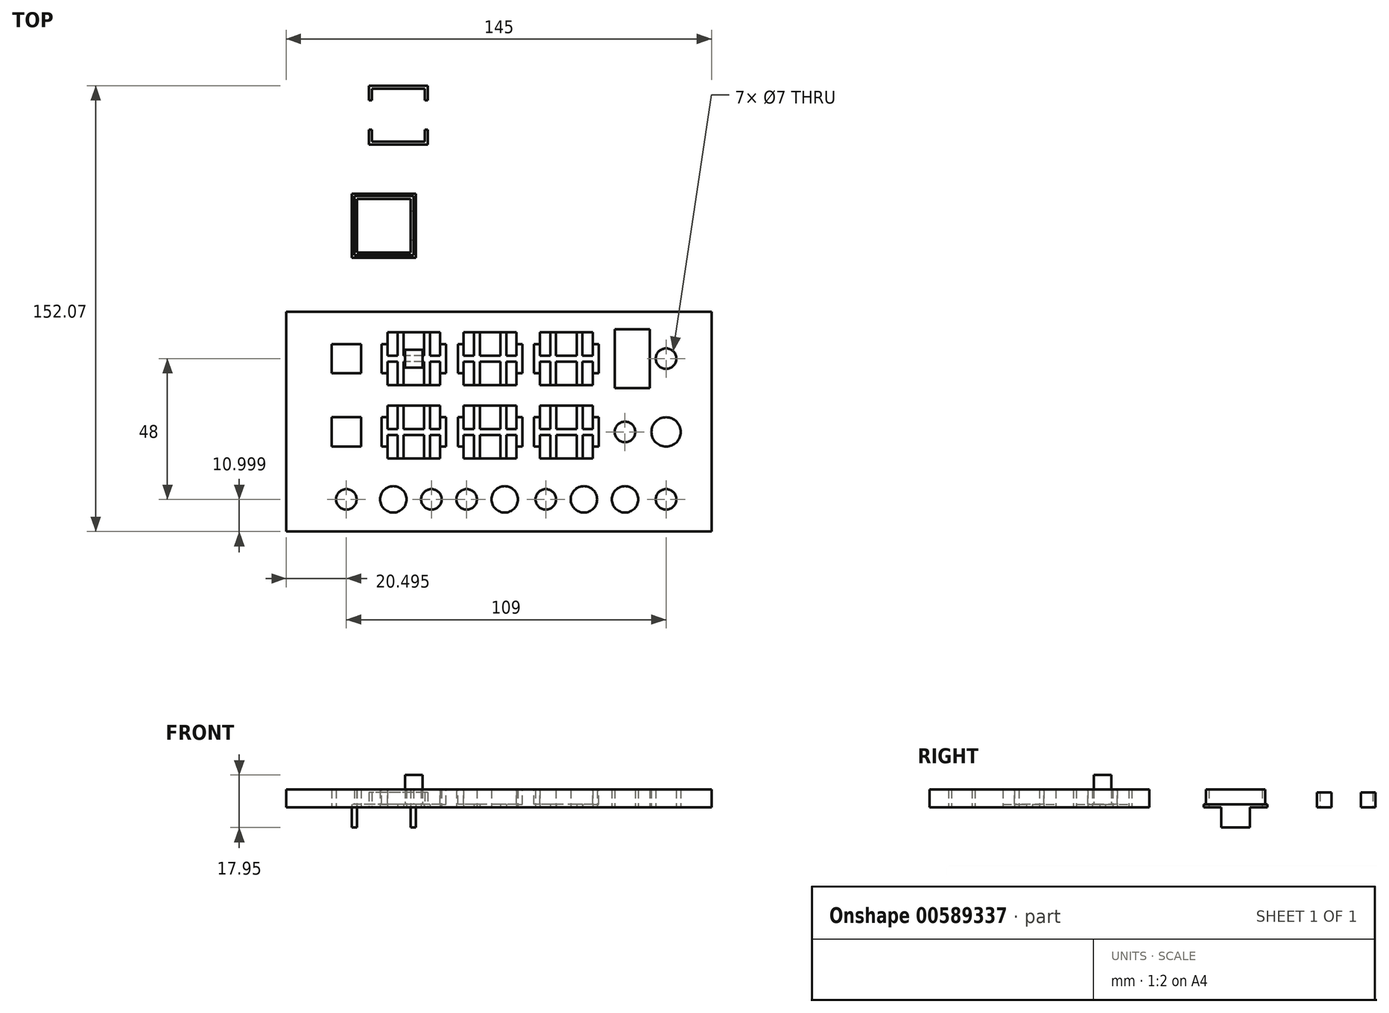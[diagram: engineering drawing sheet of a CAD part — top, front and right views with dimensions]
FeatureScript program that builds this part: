
annotation { "Feature Type Name" : "Feature", "Feature Type Description" : "" }
export const myFeature = defineFeature(function(context is Context, id is Id, definition is map)
    precondition{}
    {
        {
            var Q0;
            Q0=qCreatedBy(makeId("Top.planeOp"),FACE);
            var sketch = newSketch(context, id + "F0", { "sketchPlane" : qUnion([Q0])});
            skLineSegment(sketch, "E0.bottom", {"start": v(-10, -55.04) * mm, "end": v(-155, -55.04) * mm});
            skLineSegment(sketch, "E0.top", {"start": v(-10, 19.96) * mm, "end": v(-155, 19.96) * mm});
            skLineSegment(sketch, "E0.left", {"start": v(-10, -55.04) * mm, "end": v(-10, 19.96) * mm});
            skLineSegment(sketch, "E0.right", {"start": v(-155, -55.04) * mm, "end": v(-155, 19.96) * mm});
            skPoint(sketch, "E0.middle", {"position": v(-82.5, -17.54) * mm});
            skLineSegment(sketch, "E1.bottom", {"start": v(-101.5, -6.04) * mm, "end": v(-121.5, -6.04) * mm, "construction": true});
            skLineSegment(sketch, "E1.top", {"start": v(-101.5, 13.96) * mm, "end": v(-121.5, 13.96) * mm, "construction": true});
            skLineSegment(sketch, "E1.left", {"start": v(-101.5, -6.04) * mm, "end": v(-101.5, 13.96) * mm, "construction": true});
            skLineSegment(sketch, "E1.right", {"start": v(-121.5, -6.04) * mm, "end": v(-121.5, 13.96) * mm, "construction": true});
            skPoint(sketch, "E1.middle", {"position": v(-111.5, 3.96) * mm});
            skLineSegment(sketch, "E2.1.0.0", {"start": v(-95.5, -6.04) * mm, "end": v(-95.5, 13.96) * mm, "construction": true});
            skPoint(sketch, "E2.1.0.1", {"position": v(-85.5, 3.96) * mm});
            skLineSegment(sketch, "E2.1.0.2", {"start": v(-75.5, -6.04) * mm, "end": v(-95.5, -6.04) * mm, "construction": true});
            skLineSegment(sketch, "E2.1.0.3", {"start": v(-75.5, -6.04) * mm, "end": v(-75.5, 13.96) * mm, "construction": true});
            skLineSegment(sketch, "E2.1.0.4", {"start": v(-75.5, 13.96) * mm, "end": v(-95.5, 13.96) * mm, "construction": true});
            skLineSegment(sketch, "E2.2.0.0", {"start": v(-69.5, -6.04) * mm, "end": v(-69.5, 13.96) * mm, "construction": true});
            skPoint(sketch, "E2.2.0.1", {"position": v(-59.5, 3.96) * mm});
            skLineSegment(sketch, "E2.2.0.2", {"start": v(-49.5, -6.04) * mm, "end": v(-69.5, -6.04) * mm, "construction": true});
            skLineSegment(sketch, "E2.2.0.3", {"start": v(-49.5, -6.04) * mm, "end": v(-49.5, 13.96) * mm, "construction": true});
            skLineSegment(sketch, "E2.2.0.4", {"start": v(-49.5, 13.96) * mm, "end": v(-69.5, 13.96) * mm, "construction": true});
            skLineSegment(sketch, "E2.direction1", {"start": v(-121.5, -6.04) * mm, "end": v(-95.5, -6.04) * mm, "construction": true});
            skLineSegment(sketch, "E3.bottom", {"start": v(-101.5, -31.04) * mm, "end": v(-121.5, -31.04) * mm, "construction": true});
            skLineSegment(sketch, "E3.top", {"start": v(-101.5, -11.04) * mm, "end": v(-121.5, -11.04) * mm, "construction": true});
            skLineSegment(sketch, "E3.left", {"start": v(-101.5, -31.04) * mm, "end": v(-101.5, -11.04) * mm, "construction": true});
            skLineSegment(sketch, "E3.right", {"start": v(-121.5, -31.04) * mm, "end": v(-121.5, -11.04) * mm, "construction": true});
            skPoint(sketch, "E3.middle", {"position": v(-111.5, -21.04) * mm});
            skLineSegment(sketch, "E4.1.0.0", {"start": v(-75.5, -31.04) * mm, "end": v(-95.5, -31.04) * mm, "construction": true});
            skLineSegment(sketch, "E4.1.0.1", {"start": v(-75.5, -31.04) * mm, "end": v(-75.5, -11.04) * mm, "construction": true});
            skLineSegment(sketch, "E4.1.0.2", {"start": v(-95.5, -31.04) * mm, "end": v(-95.5, -11.04) * mm, "construction": true});
            skLineSegment(sketch, "E4.1.0.3", {"start": v(-75.5, -11.04) * mm, "end": v(-95.5, -11.04) * mm, "construction": true});
            skPoint(sketch, "E4.1.0.4", {"position": v(-85.5, -21.04) * mm});
            skLineSegment(sketch, "E4.2.0.0", {"start": v(-49.5, -31.04) * mm, "end": v(-69.5, -31.04) * mm, "construction": true});
            skLineSegment(sketch, "E4.2.0.1", {"start": v(-49.5, -31.04) * mm, "end": v(-49.5, -11.04) * mm, "construction": true});
            skLineSegment(sketch, "E4.2.0.2", {"start": v(-69.5, -31.04) * mm, "end": v(-69.5, -11.04) * mm, "construction": true});
            skLineSegment(sketch, "E4.2.0.3", {"start": v(-49.5, -11.04) * mm, "end": v(-69.5, -11.04) * mm, "construction": true});
            skPoint(sketch, "E4.2.0.4", {"position": v(-59.5, -21.04) * mm});
            skLineSegment(sketch, "E4.direction1", {"start": v(-121.5, -31.04) * mm, "end": v(-95.5, -31.04) * mm, "construction": true});
            skCircle(sketch, "E5", {"center": v(-134.5, -44.04) * mm, "radius": 3.5 * mm});
            skCircle(sketch, "E6", {"center": v(-105.5, -44.04) * mm, "radius": 3.5 * mm});
            skCircle(sketch, "E7", {"center": v(-93.5, -44.04) * mm, "radius": 3.5 * mm});
            skLineSegment(sketch, "E8.bottom", {"start": v(-155, 19.96) * mm, "end": v(-147, 19.96) * mm, "construction": true});
            skLineSegment(sketch, "E8.top", {"start": v(-155, -55.04) * mm, "end": v(-147, -55.04) * mm, "construction": true});
            skLineSegment(sketch, "E8.left", {"start": v(-155, 19.96) * mm, "end": v(-155, -55.04) * mm, "construction": true});
            skLineSegment(sketch, "E8.right", {"start": v(-147, 19.96) * mm, "end": v(-147, -55.04) * mm, "construction": true});
            skLineSegment(sketch, "E9.bottom", {"start": v(-10, -55.04) * mm, "end": v(-18, -55.04) * mm, "construction": true});
            skLineSegment(sketch, "E9.top", {"start": v(-10, 19.96) * mm, "end": v(-18, 19.96) * mm, "construction": true});
            skLineSegment(sketch, "E9.left", {"start": v(-10, -55.04) * mm, "end": v(-10, 19.96) * mm, "construction": true});
            skLineSegment(sketch, "E9.right", {"start": v(-18, -55.04) * mm, "end": v(-18, 19.96) * mm, "construction": true});
            skCircle(sketch, "E10", {"center": v(-118.5, -44.04) * mm, "radius": 4.5 * mm});
            skCircle(sketch, "E11", {"center": v(-80.5, -44.04) * mm, "radius": 4.5 * mm});
            skCircle(sketch, "E12", {"center": v(-66.5, -44.04) * mm, "radius": 3.5 * mm});
            skCircle(sketch, "E13", {"center": v(-53.5, -44.04) * mm, "radius": 4.5 * mm});
            skCircle(sketch, "E14", {"center": v(-39.5, -44.04) * mm, "radius": 4.5 * mm});
            skCircle(sketch, "E15", {"center": v(-25.5, -44.04) * mm, "radius": 3.5 * mm});
            skCircle(sketch, "E16", {"center": v(-39.5, -21.04) * mm, "radius": 3.5 * mm});
            skLineSegment(sketch, "E17.bottom", {"start": v(-31, -6.04) * mm, "end": v(-43, -6.04) * mm});
            skLineSegment(sketch, "E17.top", {"start": v(-31, 13.96) * mm, "end": v(-43, 13.96) * mm});
            skLineSegment(sketch, "E17.left", {"start": v(-31, -6.04) * mm, "end": v(-31, 13.96) * mm});
            skLineSegment(sketch, "E17.right", {"start": v(-43, -6.04) * mm, "end": v(-43, 13.96) * mm});
            skPoint(sketch, "E17.middle", {"position": v(-37, 3.96) * mm});
            skCircle(sketch, "E18", {"center": v(-25.5, 3.96) * mm, "radius": 3.5 * mm});
            skCircle(sketch, "E19", {"center": v(-25.5, -21.04) * mm, "radius": 5 * mm});
            skPoint(sketch, "E20.centerSnap0", {"position": v(-121.5, -21.04) * mm});
            skLineSegment(sketch, "E21.bottom", {"start": v(-102.5, -5.04) * mm, "end": v(-120.5, -5.04) * mm});
            skLineSegment(sketch, "E21.top", {"start": v(-102.5, 12.96) * mm, "end": v(-120.5, 12.96) * mm});
            skLineSegment(sketch, "E21.left", {"start": v(-102.5, -5.04) * mm, "end": v(-102.5, 12.96) * mm});
            skLineSegment(sketch, "E21.right", {"start": v(-120.5, -5.04) * mm, "end": v(-120.5, 12.96) * mm});
            skLineSegment(sketch, "E22.bottom", {"start": v(-102.5, -30.04) * mm, "end": v(-120.5, -30.04) * mm});
            skLineSegment(sketch, "E22.top", {"start": v(-102.5, -12.04) * mm, "end": v(-120.5, -12.04) * mm});
            skLineSegment(sketch, "E22.left", {"start": v(-102.5, -30.04) * mm, "end": v(-102.5, -12.04) * mm});
            skLineSegment(sketch, "E22.right", {"start": v(-120.5, -30.04) * mm, "end": v(-120.5, -12.04) * mm});
            skLineSegment(sketch, "E23.bottom", {"start": v(-102.5, 2.96) * mm, "end": v(-106, 2.96) * mm});
            skLineSegment(sketch, "E23.top", {"start": v(-102.5, 4.96) * mm, "end": v(-106, 4.96) * mm});
            skLineSegment(sketch, "E23.left", {"start": v(-102.5, 2.96) * mm, "end": v(-102.5, 4.96) * mm});
            skLineSegment(sketch, "E23.right", {"start": v(-120.5, 2.96) * mm, "end": v(-120.5, 4.96) * mm});
            skLineSegment(sketch, "E24.bottom", {"start": v(-115, -5.04) * mm, "end": v(-117, -5.04) * mm});
            skLineSegment(sketch, "E24.top", {"start": v(-115, 12.96) * mm, "end": v(-117, 12.96) * mm});
            skLineSegment(sketch, "E24.left", {"start": v(-115, -5.04) * mm, "end": v(-115, 2.96) * mm});
            skLineSegment(sketch, "E24.right", {"start": v(-117, -5.04) * mm, "end": v(-117, 2.96) * mm});
            skPoint(sketch, "E24.middle", {"position": v(-116, 3.96) * mm});
            skLineSegment(sketch, "E25.bottom", {"start": v(-106, -5.04) * mm, "end": v(-108, -5.04) * mm});
            skLineSegment(sketch, "E25.top", {"start": v(-106, 12.96) * mm, "end": v(-108, 12.96) * mm});
            skLineSegment(sketch, "E25.left", {"start": v(-106, -5.04) * mm, "end": v(-106, 2.96) * mm});
            skLineSegment(sketch, "E25.right", {"start": v(-108, -5.04) * mm, "end": v(-108, 2.96) * mm});
            skPoint(sketch, "E25.middle", {"position": v(-107, 3.96) * mm});
            skLineSegment(sketch, "E26.trimOffspring", {"start": v(-117, 4.96) * mm, "end": v(-117, 12.96) * mm});
            skLineSegment(sketch, "E27.trimOffspring", {"start": v(-117, 4.96) * mm, "end": v(-120.5, 4.96) * mm});
            skLineSegment(sketch, "E28.trimOffspring", {"start": v(-115, 4.96) * mm, "end": v(-115, 12.96) * mm});
            skLineSegment(sketch, "E29.trimOffspring", {"start": v(-117, 2.96) * mm, "end": v(-120.5, 2.96) * mm});
            skLineSegment(sketch, "E30.trimOffspring", {"start": v(-108, 4.96) * mm, "end": v(-108, 12.96) * mm});
            skLineSegment(sketch, "E31.trimOffspring", {"start": v(-108, 4.96) * mm, "end": v(-115, 4.96) * mm});
            skLineSegment(sketch, "E32.trimOffspring", {"start": v(-106, 4.96) * mm, "end": v(-106, 12.96) * mm});
            skLineSegment(sketch, "E33.trimOffspring", {"start": v(-108, 2.96) * mm, "end": v(-115, 2.96) * mm});
            skLineSegment(sketch, "E34.bottom", {"start": v(-131, -50.54) * mm, "end": v(-138, -50.54) * mm, "construction": true});
            skLineSegment(sketch, "E34.top", {"start": v(-131, -37.54) * mm, "end": v(-138, -37.54) * mm, "construction": true});
            skLineSegment(sketch, "E34.left", {"start": v(-131, -50.54) * mm, "end": v(-131, -37.54) * mm, "construction": true});
            skLineSegment(sketch, "E34.right", {"start": v(-138, -50.54) * mm, "end": v(-138, -37.54) * mm, "construction": true});
            skLineSegment(sketch, "E35.bottom", {"start": v(-102.5, -22.04) * mm, "end": v(-105.98, -22.04) * mm});
            skLineSegment(sketch, "E35.top", {"start": v(-102.5, -20.04) * mm, "end": v(-105.98, -20.04) * mm});
            skLineSegment(sketch, "E35.left", {"start": v(-102.5, -22.04) * mm, "end": v(-102.5, -20.04) * mm});
            skLineSegment(sketch, "E35.right", {"start": v(-120.5, -22.04) * mm, "end": v(-120.5, -20.04) * mm});
            skLineSegment(sketch, "E36.bottom", {"start": v(-114.98, -30.04) * mm, "end": v(-116.98, -30.04) * mm});
            skLineSegment(sketch, "E36.top", {"start": v(-114.98, -12.04) * mm, "end": v(-116.98, -12.04) * mm});
            skLineSegment(sketch, "E36.left", {"start": v(-114.98, -30.04) * mm, "end": v(-114.98, -22.04) * mm});
            skLineSegment(sketch, "E36.right", {"start": v(-116.98, -30.04) * mm, "end": v(-116.98, -22.04) * mm});
            skPoint(sketch, "E36.middle", {"position": v(-115.98, -21.04) * mm});
            skLineSegment(sketch, "E37.bottom", {"start": v(-105.98, -30.04) * mm, "end": v(-107.98, -30.04) * mm});
            skLineSegment(sketch, "E37.top", {"start": v(-105.98, -12.04) * mm, "end": v(-107.98, -12.04) * mm});
            skLineSegment(sketch, "E37.left", {"start": v(-105.98, -30.04) * mm, "end": v(-105.98, -22.04) * mm});
            skLineSegment(sketch, "E37.right", {"start": v(-107.98, -30.04) * mm, "end": v(-107.98, -22.04) * mm});
            skPoint(sketch, "E37.middle", {"position": v(-106.98, -21.04) * mm});
            skLineSegment(sketch, "E38.trimOffspring", {"start": v(-116.98, -20.04) * mm, "end": v(-116.98, -12.04) * mm});
            skLineSegment(sketch, "E39.trimOffspring", {"start": v(-116.98, -20.04) * mm, "end": v(-120.5, -20.04) * mm});
            skLineSegment(sketch, "E40.trimOffspring", {"start": v(-114.98, -20.04) * mm, "end": v(-114.98, -12.04) * mm});
            skLineSegment(sketch, "E41.trimOffspring", {"start": v(-116.98, -22.04) * mm, "end": v(-120.5, -22.04) * mm});
            skLineSegment(sketch, "E42.trimOffspring", {"start": v(-107.98, -20.04) * mm, "end": v(-107.98, -12.04) * mm});
            skLineSegment(sketch, "E43.trimOffspring", {"start": v(-107.98, -20.04) * mm, "end": v(-114.98, -20.04) * mm});
            skLineSegment(sketch, "E44.trimOffspring", {"start": v(-105.98, -20.04) * mm, "end": v(-105.98, -12.04) * mm});
            skLineSegment(sketch, "E45.trimOffspring", {"start": v(-107.98, -22.04) * mm, "end": v(-114.98, -22.04) * mm});
            skLineSegment(sketch, "E46.bottom", {"start": v(-129.5, -1.04) * mm, "end": v(-139.5, -1.04) * mm});
            skLineSegment(sketch, "E46.top", {"start": v(-129.5, 8.96) * mm, "end": v(-139.5, 8.96) * mm});
            skLineSegment(sketch, "E46.left", {"start": v(-129.5, -1.04) * mm, "end": v(-129.5, 8.96) * mm});
            skLineSegment(sketch, "E46.right", {"start": v(-139.5, -1.04) * mm, "end": v(-139.5, 8.96) * mm});
            skPoint(sketch, "E46.middle", {"position": v(-134.5, 3.96) * mm});
            skLineSegment(sketch, "E47.bottom", {"start": v(-129.5, -26.04) * mm, "end": v(-139.5, -26.04) * mm});
            skLineSegment(sketch, "E47.top", {"start": v(-129.5, -16.04) * mm, "end": v(-139.5, -16.04) * mm});
            skLineSegment(sketch, "E47.left", {"start": v(-129.5, -26.04) * mm, "end": v(-129.5, -16.04) * mm});
            skLineSegment(sketch, "E47.right", {"start": v(-139.5, -26.04) * mm, "end": v(-139.5, -16.04) * mm});
            skPoint(sketch, "E47.middle", {"position": v(-134.5, -21.04) * mm});
            skLineSegment(sketch, "E48.1.0.0", {"start": v(-91, 4.96) * mm, "end": v(-91, 12.96) * mm});
            skLineSegment(sketch, "E48.1.0.2", {"start": v(-76.5, -5.04) * mm, "end": v(-76.5, 12.96) * mm});
            skLineSegment(sketch, "E48.1.0.3", {"start": v(-80, -5.04) * mm, "end": v(-80, 2.96) * mm});
            skPoint(sketch, "E48.1.0.4", {"position": v(-90, 3.96) * mm});
            skLineSegment(sketch, "E48.1.0.5", {"start": v(-82, 4.96) * mm, "end": v(-82, 12.96) * mm});
            skLineSegment(sketch, "E48.1.0.6", {"start": v(-80, 4.96) * mm, "end": v(-80, 12.96) * mm});
            skLineSegment(sketch, "E48.1.0.7", {"start": v(-82, 4.96) * mm, "end": v(-89, 4.96) * mm});
            skLineSegment(sketch, "E48.1.0.8", {"start": v(-76.5, 4.96) * mm, "end": v(-80, 4.96) * mm});
            skLineSegment(sketch, "E48.1.0.9", {"start": v(-76.5, 2.96) * mm, "end": v(-80, 2.96) * mm});
            skLineSegment(sketch, "E48.1.0.10", {"start": v(-80, 12.96) * mm, "end": v(-82, 12.96) * mm});
            skPoint(sketch, "E48.1.0.11", {"position": v(-81, 3.96) * mm});
            skLineSegment(sketch, "E48.1.0.12", {"start": v(-91, 4.96) * mm, "end": v(-94.5, 4.96) * mm});
            skLineSegment(sketch, "E48.1.0.13", {"start": v(-91, 2.96) * mm, "end": v(-94.5, 2.96) * mm});
            skLineSegment(sketch, "E48.1.0.14", {"start": v(-89, 4.96) * mm, "end": v(-89, 12.96) * mm});
            skLineSegment(sketch, "E48.1.0.15", {"start": v(-76.5, 12.96) * mm, "end": v(-94.5, 12.96) * mm});
            skLineSegment(sketch, "E48.1.0.16", {"start": v(-91, -5.04) * mm, "end": v(-91, 2.96) * mm});
            skLineSegment(sketch, "E48.1.0.17", {"start": v(-76.5, -5.04) * mm, "end": v(-94.5, -5.04) * mm});
            skLineSegment(sketch, "E48.1.0.18", {"start": v(-89, -5.04) * mm, "end": v(-89, 2.96) * mm});
            skLineSegment(sketch, "E48.1.0.19", {"start": v(-82, -5.04) * mm, "end": v(-82, 2.96) * mm});
            skLineSegment(sketch, "E48.1.0.20", {"start": v(-94.5, -5.04) * mm, "end": v(-94.5, 12.96) * mm});
            skLineSegment(sketch, "E48.1.0.21", {"start": v(-82, 2.96) * mm, "end": v(-89, 2.96) * mm});
            skLineSegment(sketch, "E48.1.0.22", {"start": v(-80, -5.04) * mm, "end": v(-82, -5.04) * mm});
            skLineSegment(sketch, "E48.1.0.23", {"start": v(-76.5, 2.96) * mm, "end": v(-76.5, 4.96) * mm});
            skLineSegment(sketch, "E48.1.0.24", {"start": v(-89, -5.04) * mm, "end": v(-91, -5.04) * mm});
            skLineSegment(sketch, "E48.1.0.25", {"start": v(-94.5, 2.96) * mm, "end": v(-94.5, 4.96) * mm});
            skLineSegment(sketch, "E48.1.0.27", {"start": v(-89, 12.96) * mm, "end": v(-91, 12.96) * mm});
            skLineSegment(sketch, "E48.2.0.0", {"start": v(-65, 4.96) * mm, "end": v(-65, 12.96) * mm});
            skLineSegment(sketch, "E48.2.0.2", {"start": v(-50.5, -5.04) * mm, "end": v(-50.5, 12.96) * mm});
            skLineSegment(sketch, "E48.2.0.3", {"start": v(-54, -5.04) * mm, "end": v(-54, 2.96) * mm});
            skPoint(sketch, "E48.2.0.4", {"position": v(-64, 3.96) * mm});
            skLineSegment(sketch, "E48.2.0.5", {"start": v(-56, 4.96) * mm, "end": v(-56, 12.96) * mm});
            skLineSegment(sketch, "E48.2.0.6", {"start": v(-54, 4.96) * mm, "end": v(-54, 12.96) * mm});
            skLineSegment(sketch, "E48.2.0.7", {"start": v(-56, 4.96) * mm, "end": v(-63, 4.96) * mm});
            skLineSegment(sketch, "E48.2.0.8", {"start": v(-50.5, 4.96) * mm, "end": v(-54, 4.96) * mm});
            skLineSegment(sketch, "E48.2.0.9", {"start": v(-50.5, 2.96) * mm, "end": v(-54, 2.96) * mm});
            skLineSegment(sketch, "E48.2.0.10", {"start": v(-54, 12.96) * mm, "end": v(-56, 12.96) * mm});
            skPoint(sketch, "E48.2.0.11", {"position": v(-55, 3.96) * mm});
            skLineSegment(sketch, "E48.2.0.12", {"start": v(-65, 4.96) * mm, "end": v(-68.5, 4.96) * mm});
            skLineSegment(sketch, "E48.2.0.13", {"start": v(-65, 2.96) * mm, "end": v(-68.5, 2.96) * mm});
            skLineSegment(sketch, "E48.2.0.14", {"start": v(-63, 4.96) * mm, "end": v(-63, 12.96) * mm});
            skLineSegment(sketch, "E48.2.0.15", {"start": v(-50.5, 12.96) * mm, "end": v(-68.5, 12.96) * mm});
            skLineSegment(sketch, "E48.2.0.16", {"start": v(-65, -5.04) * mm, "end": v(-65, 2.96) * mm});
            skLineSegment(sketch, "E48.2.0.17", {"start": v(-50.5, -5.04) * mm, "end": v(-68.5, -5.04) * mm});
            skLineSegment(sketch, "E48.2.0.18", {"start": v(-63, -5.04) * mm, "end": v(-63, 2.96) * mm});
            skLineSegment(sketch, "E48.2.0.19", {"start": v(-56, -5.04) * mm, "end": v(-56, 2.96) * mm});
            skLineSegment(sketch, "E48.2.0.20", {"start": v(-68.5, -5.04) * mm, "end": v(-68.5, 12.96) * mm});
            skLineSegment(sketch, "E48.2.0.21", {"start": v(-56, 2.96) * mm, "end": v(-63, 2.96) * mm});
            skLineSegment(sketch, "E48.2.0.22", {"start": v(-54, -5.04) * mm, "end": v(-56, -5.04) * mm});
            skLineSegment(sketch, "E48.2.0.23", {"start": v(-50.5, 2.96) * mm, "end": v(-50.5, 4.96) * mm});
            skLineSegment(sketch, "E48.2.0.24", {"start": v(-63, -5.04) * mm, "end": v(-65, -5.04) * mm});
            skLineSegment(sketch, "E48.2.0.25", {"start": v(-68.5, 2.96) * mm, "end": v(-68.5, 4.96) * mm});
            skLineSegment(sketch, "E48.2.0.27", {"start": v(-63, 12.96) * mm, "end": v(-65, 12.96) * mm});
            skLineSegment(sketch, "E48.direction1", {"start": v(-120.5, -5.04) * mm, "end": v(-94.5, -5.04) * mm, "construction": true});
            skLineSegment(sketch, "E49.1.0.0", {"start": v(-76.5, -20.04) * mm, "end": v(-79.98, -20.04) * mm});
            skLineSegment(sketch, "E49.1.0.1", {"start": v(-88.98, -20.04) * mm, "end": v(-88.98, -12.04) * mm});
            skLineSegment(sketch, "E49.1.0.2", {"start": v(-81.98, -30.04) * mm, "end": v(-81.98, -22.04) * mm});
            skLineSegment(sketch, "E49.1.0.3", {"start": v(-94.5, -30.04) * mm, "end": v(-94.5, -12.04) * mm});
            skLineSegment(sketch, "E49.1.0.4", {"start": v(-90.98, -30.04) * mm, "end": v(-90.98, -22.04) * mm});
            skLineSegment(sketch, "E49.1.0.5", {"start": v(-76.5, -30.04) * mm, "end": v(-76.5, -12.04) * mm});
            skLineSegment(sketch, "E49.1.0.6", {"start": v(-81.98, -22.04) * mm, "end": v(-88.98, -22.04) * mm});
            skLineSegment(sketch, "E49.1.0.7", {"start": v(-88.98, -30.04) * mm, "end": v(-88.98, -22.04) * mm});
            skLineSegment(sketch, "E49.1.0.9", {"start": v(-79.98, -20.04) * mm, "end": v(-79.98, -12.04) * mm});
            skLineSegment(sketch, "E49.1.0.10", {"start": v(-76.5, -22.04) * mm, "end": v(-79.98, -22.04) * mm});
            skPoint(sketch, "E49.1.0.11", {"position": v(-80.98, -21.04) * mm});
            skLineSegment(sketch, "E49.1.0.12", {"start": v(-90.98, -22.04) * mm, "end": v(-94.5, -22.04) * mm});
            skLineSegment(sketch, "E49.1.0.14", {"start": v(-81.98, -20.04) * mm, "end": v(-88.98, -20.04) * mm});
            skPoint(sketch, "E49.1.0.15", {"position": v(-89.98, -21.04) * mm});
            skLineSegment(sketch, "E49.1.0.16", {"start": v(-79.98, -30.04) * mm, "end": v(-79.98, -22.04) * mm});
            skLineSegment(sketch, "E49.1.0.17", {"start": v(-76.5, -30.04) * mm, "end": v(-94.5, -30.04) * mm});
            skLineSegment(sketch, "E49.1.0.18", {"start": v(-90.98, -20.04) * mm, "end": v(-90.98, -12.04) * mm});
            skLineSegment(sketch, "E49.1.0.19", {"start": v(-81.98, -20.04) * mm, "end": v(-81.98, -12.04) * mm});
            skLineSegment(sketch, "E49.1.0.20", {"start": v(-90.98, -20.04) * mm, "end": v(-94.5, -20.04) * mm});
            skLineSegment(sketch, "E49.1.0.21", {"start": v(-76.5, -12.04) * mm, "end": v(-94.5, -12.04) * mm});
            skLineSegment(sketch, "E49.1.0.22", {"start": v(-88.98, -12.04) * mm, "end": v(-90.98, -12.04) * mm});
            skLineSegment(sketch, "E49.1.0.23", {"start": v(-76.5, -22.04) * mm, "end": v(-76.5, -20.04) * mm});
            skLineSegment(sketch, "E49.1.0.24", {"start": v(-94.5, -22.04) * mm, "end": v(-94.5, -20.04) * mm});
            skLineSegment(sketch, "E49.1.0.26", {"start": v(-94.5, -30.04) * mm, "end": v(-94.5, -12.04) * mm});
            skLineSegment(sketch, "E49.1.0.27", {"start": v(-79.98, -12.04) * mm, "end": v(-81.98, -12.04) * mm});
            skLineSegment(sketch, "E49.1.0.28", {"start": v(-76.5, -30.04) * mm, "end": v(-94.5, -30.04) * mm});
            skLineSegment(sketch, "E49.1.0.29", {"start": v(-76.5, -12.04) * mm, "end": v(-94.5, -12.04) * mm});
            skLineSegment(sketch, "E49.1.0.30", {"start": v(-76.5, -30.04) * mm, "end": v(-76.5, -12.04) * mm});
            skLineSegment(sketch, "E49.1.0.31", {"start": v(-88.98, -30.04) * mm, "end": v(-90.98, -30.04) * mm});
            skLineSegment(sketch, "E49.1.0.32", {"start": v(-79.98, -30.04) * mm, "end": v(-81.98, -30.04) * mm});
            skLineSegment(sketch, "E49.2.0.0", {"start": v(-50.5, -20.04) * mm, "end": v(-53.98, -20.04) * mm});
            skLineSegment(sketch, "E49.2.0.1", {"start": v(-62.98, -20.04) * mm, "end": v(-62.98, -12.04) * mm});
            skLineSegment(sketch, "E49.2.0.2", {"start": v(-55.98, -30.04) * mm, "end": v(-55.98, -22.04) * mm});
            skLineSegment(sketch, "E49.2.0.3", {"start": v(-68.5, -30.04) * mm, "end": v(-68.5, -12.04) * mm});
            skLineSegment(sketch, "E49.2.0.4", {"start": v(-64.98, -30.04) * mm, "end": v(-64.98, -22.04) * mm});
            skLineSegment(sketch, "E49.2.0.5", {"start": v(-50.5, -30.04) * mm, "end": v(-50.5, -12.04) * mm});
            skLineSegment(sketch, "E49.2.0.6", {"start": v(-55.98, -22.04) * mm, "end": v(-62.98, -22.04) * mm});
            skLineSegment(sketch, "E49.2.0.7", {"start": v(-62.98, -30.04) * mm, "end": v(-62.98, -22.04) * mm});
            skLineSegment(sketch, "E49.2.0.9", {"start": v(-53.98, -20.04) * mm, "end": v(-53.98, -12.04) * mm});
            skLineSegment(sketch, "E49.2.0.10", {"start": v(-50.5, -22.04) * mm, "end": v(-53.98, -22.04) * mm});
            skPoint(sketch, "E49.2.0.11", {"position": v(-54.98, -21.04) * mm});
            skLineSegment(sketch, "E49.2.0.12", {"start": v(-64.98, -22.04) * mm, "end": v(-68.5, -22.04) * mm});
            skLineSegment(sketch, "E49.2.0.14", {"start": v(-55.98, -20.04) * mm, "end": v(-62.98, -20.04) * mm});
            skPoint(sketch, "E49.2.0.15", {"position": v(-63.98, -21.04) * mm});
            skLineSegment(sketch, "E49.2.0.16", {"start": v(-53.98, -30.04) * mm, "end": v(-53.98, -22.04) * mm});
            skLineSegment(sketch, "E49.2.0.17", {"start": v(-50.5, -30.04) * mm, "end": v(-68.5, -30.04) * mm});
            skLineSegment(sketch, "E49.2.0.18", {"start": v(-64.98, -20.04) * mm, "end": v(-64.98, -12.04) * mm});
            skLineSegment(sketch, "E49.2.0.19", {"start": v(-55.98, -20.04) * mm, "end": v(-55.98, -12.04) * mm});
            skLineSegment(sketch, "E49.2.0.20", {"start": v(-64.98, -20.04) * mm, "end": v(-68.5, -20.04) * mm});
            skLineSegment(sketch, "E49.2.0.21", {"start": v(-50.5, -12.04) * mm, "end": v(-68.5, -12.04) * mm});
            skLineSegment(sketch, "E49.2.0.22", {"start": v(-62.98, -12.04) * mm, "end": v(-64.98, -12.04) * mm});
            skLineSegment(sketch, "E49.2.0.23", {"start": v(-50.5, -22.04) * mm, "end": v(-50.5, -20.04) * mm});
            skLineSegment(sketch, "E49.2.0.24", {"start": v(-68.5, -22.04) * mm, "end": v(-68.5, -20.04) * mm});
            skLineSegment(sketch, "E49.2.0.26", {"start": v(-68.5, -30.04) * mm, "end": v(-68.5, -12.04) * mm});
            skLineSegment(sketch, "E49.2.0.27", {"start": v(-53.98, -12.04) * mm, "end": v(-55.98, -12.04) * mm});
            skLineSegment(sketch, "E49.2.0.28", {"start": v(-50.5, -30.04) * mm, "end": v(-68.5, -30.04) * mm});
            skLineSegment(sketch, "E49.2.0.29", {"start": v(-50.5, -12.04) * mm, "end": v(-68.5, -12.04) * mm});
            skLineSegment(sketch, "E49.2.0.30", {"start": v(-50.5, -30.04) * mm, "end": v(-50.5, -12.04) * mm});
            skLineSegment(sketch, "E49.2.0.31", {"start": v(-62.98, -30.04) * mm, "end": v(-64.98, -30.04) * mm});
            skLineSegment(sketch, "E49.2.0.32", {"start": v(-53.98, -30.04) * mm, "end": v(-55.98, -30.04) * mm});
            skLineSegment(sketch, "E49.direction1", {"start": v(-120.5, -30.04) * mm, "end": v(-94.5, -30.04) * mm, "construction": true});
            skLineSegment(sketch, "E50.bottom", {"start": v(-133, -1.04) * mm, "end": v(-136, -1.04) * mm});
            skLineSegment(sketch, "E50.top", {"start": v(-133, 8.96) * mm, "end": v(-136, 8.96) * mm});
            skLineSegment(sketch, "E50.left", {"start": v(-133, -1.04) * mm, "end": v(-133, 8.96) * mm});
            skLineSegment(sketch, "E50.right", {"start": v(-136, -1.04) * mm, "end": v(-136, 8.96) * mm});
            skLineSegment(sketch, "E51.bottom", {"start": v(-133, -26.04) * mm, "end": v(-136, -26.04) * mm});
            skLineSegment(sketch, "E51.top", {"start": v(-133, -16.04) * mm, "end": v(-136, -16.04) * mm});
            skLineSegment(sketch, "E51.left", {"start": v(-133, -26.04) * mm, "end": v(-133, -16.04) * mm});
            skLineSegment(sketch, "E51.right", {"start": v(-136, -26.04) * mm, "end": v(-136, -16.04) * mm});
            skSolve(sketch);
        }
        {
            var Q0;
            Q0=makeQuery(id+"F0.imprint","IMPRINT",FACE,{"disambiguationData":[TD([[makeQuery(id+"F0.imprint","IMPRINT",EDGE,{"derivedFrom":sQuery(id+"F0.wireOp",EDGE,"E0.bottom")}),-1.0]])]});
            var Q1;
            Q1=makeQuery(id+"F0.imprint","IMPRINT",FACE,{"disambiguationData":[TD([[makeQuery(id+"F0.imprint","IMPRINT",EDGE,{"derivedFrom":sQuery(id+"F0.wireOp",EDGE,"E23.bottom")}),-1.0]])]});
            var Q2;
            Q2=makeQuery(id+"F0.imprint","IMPRINT",FACE,{"disambiguationData":[TD([[makeQuery(id+"F0.imprint","IMPRINT",EDGE,{"derivedFrom":sQuery(id+"F0.wireOp",EDGE,"E35.bottom")}),-1.0]])]});
            var Q3;
            Q3=makeQuery(id+"F0.imprint","IMPRINT",FACE,{"disambiguationData":[TD([[makeQuery(id+"F0.imprint","IMPRINT",EDGE,{"derivedFrom":sQuery(id+"F0.wireOp",EDGE,"E48.1.0.0")}),-1.0]])]});
            var Q4;
            Q4=makeQuery(id+"F0.imprint","IMPRINT",FACE,{"disambiguationData":[TD([[makeQuery(id+"F0.imprint","IMPRINT",EDGE,{"derivedFrom":sQuery(id+"F0.wireOp",EDGE,"E48.2.0.0")}),-1.0]])]});
            var Q5;
            {var subQ3=sQuery(id+"F0.wireOp",EDGE,"E49.2.0.0");Q5=makeQuery(id+"F0.imprint","IMPRINT",FACE,{"disambiguationData":[TD([[makeQuery(id+"F0.imprint","IMPRINT",EDGE,{"derivedFrom":subQ3}),1.0]])]});}
            var Q6;
            {var subQ3=sQuery(id+"F0.wireOp",EDGE,"E49.1.0.0");Q6=makeQuery(id+"F0.imprint","IMPRINT",FACE,{"disambiguationData":[TD([[makeQuery(id+"F0.imprint","IMPRINT",EDGE,{"derivedFrom":subQ3}),1.0]])]});}
            var Q7;
            Q7=makeQuery(id+"F0.imprint","IMPRINT",FACE,{"disambiguationData":[TD([[makeQuery(id+"F0.imprint","IMPRINT",EDGE,{"derivedFrom":sQuery(id+"F0.wireOp",EDGE,"E50.bottom")}),-1.0]])]});
            var Q8;
            Q8=makeQuery(id+"F0.imprint","IMPRINT",FACE,{"disambiguationData":[TD([[makeQuery(id+"F0.imprint","IMPRINT",EDGE,{"derivedFrom":sQuery(id+"F0.wireOp",EDGE,"E51.bottom")}),-1.0]])]});
            extrude(context, id + "F1", {"entities" : qUnion([Q0, Q1, Q2, Q3, Q4, Q5, Q6, Q7, Q8]), "depth" : 1 * mm});
        }
        {
            var Q0;
            Q0=makeQuery(id+"F1.opExtrude","CAP_FACE",FACE,{"disambiguationData":[OSD([sQuery(id+"F0.wireOp",EDGE,"E0.bottom"),sQuery(id+"F0.wireOp",EDGE,"E0.top"),sQuery(id+"F0.wireOp",EDGE,"E0.left"),sQuery(id+"F0.wireOp",EDGE,"E0.right"),sQuery(id+"F0.wireOp",EDGE,"E5"),sQuery(id+"F0.wireOp",EDGE,"E6"),sQuery(id+"F0.wireOp",EDGE,"E7"),sQuery(id+"F0.wireOp",EDGE,"E10"),sQuery(id+"F0.wireOp",EDGE,"E11"),sQuery(id+"F0.wireOp",EDGE,"E12"),sQuery(id+"F0.wireOp",EDGE,"E13"),sQuery(id+"F0.wireOp",EDGE,"E14"),sQuery(id+"F0.wireOp",EDGE,"E15"),sQuery(id+"F0.wireOp",EDGE,"E16"),sQuery(id+"F0.wireOp",EDGE,"E17.bottom"),sQuery(id+"F0.wireOp",EDGE,"E17.top"),sQuery(id+"F0.wireOp",EDGE,"E17.left"),sQuery(id+"F0.wireOp",EDGE,"E17.right"),sQuery(id+"F0.wireOp",EDGE,"E18"),sQuery(id+"F0.wireOp",EDGE,"E19"),sQuery(id+"F0.wireOp",EDGE,"E21.bottom"),sQuery(id+"F0.wireOp",EDGE,"E21.top"),sQuery(id+"F0.wireOp",EDGE,"E21.left"),sQuery(id+"F0.wireOp",EDGE,"E21.right"),sQuery(id+"F0.wireOp",EDGE,"E23.bottom"),sQuery(id+"F0.wireOp",EDGE,"E23.top"),sQuery(id+"F0.wireOp",EDGE,"E24.left"),sQuery(id+"F0.wireOp",EDGE,"E24.right"),sQuery(id+"F0.wireOp",EDGE,"E25.left"),sQuery(id+"F0.wireOp",EDGE,"E25.right"),sQuery(id+"F0.wireOp",EDGE,"E26.trimOffspring"),sQuery(id+"F0.wireOp",EDGE,"E27.trimOffspring"),sQuery(id+"F0.wireOp",EDGE,"E28.trimOffspring"),sQuery(id+"F0.wireOp",EDGE,"E29.trimOffspring"),sQuery(id+"F0.wireOp",EDGE,"E30.trimOffspring"),sQuery(id+"F0.wireOp",EDGE,"E31.trimOffspring"),sQuery(id+"F0.wireOp",EDGE,"E32.trimOffspring"),sQuery(id+"F0.wireOp",EDGE,"E33.trimOffspring"),sQuery(id+"F0.wireOp",EDGE,"E22.bottom"),sQuery(id+"F0.wireOp",EDGE,"E22.top"),sQuery(id+"F0.wireOp",EDGE,"E22.left"),sQuery(id+"F0.wireOp",EDGE,"E22.right"),sQuery(id+"F0.wireOp",EDGE,"E35.bottom"),sQuery(id+"F0.wireOp",EDGE,"E35.top"),sQuery(id+"F0.wireOp",EDGE,"E36.left"),sQuery(id+"F0.wireOp",EDGE,"E36.right"),sQuery(id+"F0.wireOp",EDGE,"E37.left"),sQuery(id+"F0.wireOp",EDGE,"E37.right"),sQuery(id+"F0.wireOp",EDGE,"E38.trimOffspring"),sQuery(id+"F0.wireOp",EDGE,"E39.trimOffspring"),sQuery(id+"F0.wireOp",EDGE,"E40.trimOffspring"),sQuery(id+"F0.wireOp",EDGE,"E41.trimOffspring"),sQuery(id+"F0.wireOp",EDGE,"E42.trimOffspring"),sQuery(id+"F0.wireOp",EDGE,"E43.trimOffspring"),sQuery(id+"F0.wireOp",EDGE,"E44.trimOffspring"),sQuery(id+"F0.wireOp",EDGE,"E45.trimOffspring"),sQuery(id+"F0.wireOp",EDGE,"E46.bottom"),sQuery(id+"F0.wireOp",EDGE,"E46.top"),sQuery(id+"F0.wireOp",EDGE,"E46.left"),sQuery(id+"F0.wireOp",EDGE,"E46.right"),sQuery(id+"F0.wireOp",EDGE,"E47.bottom"),sQuery(id+"F0.wireOp",EDGE,"E47.top"),sQuery(id+"F0.wireOp",EDGE,"E47.left"),sQuery(id+"F0.wireOp",EDGE,"E47.right"),sQuery(id+"F0.wireOp",EDGE,"E48.1.0.0"),sQuery(id+"F0.wireOp",EDGE,"E48.1.0.2"),sQuery(id+"F0.wireOp",EDGE,"E48.1.0.3"),sQuery(id+"F0.wireOp",EDGE,"E48.1.0.5"),sQuery(id+"F0.wireOp",EDGE,"E48.1.0.6"),sQuery(id+"F0.wireOp",EDGE,"E48.1.0.7"),sQuery(id+"F0.wireOp",EDGE,"E48.1.0.8"),sQuery(id+"F0.wireOp",EDGE,"E48.1.0.9"),sQuery(id+"F0.wireOp",EDGE,"E48.1.0.12"),sQuery(id+"F0.wireOp",EDGE,"E48.1.0.13"),sQuery(id+"F0.wireOp",EDGE,"E48.1.0.14"),sQuery(id+"F0.wireOp",EDGE,"E48.1.0.15"),sQuery(id+"F0.wireOp",EDGE,"E48.1.0.16"),sQuery(id+"F0.wireOp",EDGE,"E48.1.0.17"),sQuery(id+"F0.wireOp",EDGE,"E48.1.0.18"),sQuery(id+"F0.wireOp",EDGE,"E48.1.0.19"),sQuery(id+"F0.wireOp",EDGE,"E48.1.0.20"),sQuery(id+"F0.wireOp",EDGE,"E48.1.0.21"),sQuery(id+"F0.wireOp",EDGE,"E48.2.0.0"),sQuery(id+"F0.wireOp",EDGE,"E48.2.0.2"),sQuery(id+"F0.wireOp",EDGE,"E48.2.0.3"),sQuery(id+"F0.wireOp",EDGE,"E48.2.0.5"),sQuery(id+"F0.wireOp",EDGE,"E48.2.0.6"),sQuery(id+"F0.wireOp",EDGE,"E48.2.0.7"),sQuery(id+"F0.wireOp",EDGE,"E48.2.0.8"),sQuery(id+"F0.wireOp",EDGE,"E48.2.0.9"),sQuery(id+"F0.wireOp",EDGE,"E48.2.0.12"),sQuery(id+"F0.wireOp",EDGE,"E48.2.0.13"),sQuery(id+"F0.wireOp",EDGE,"E48.2.0.14"),sQuery(id+"F0.wireOp",EDGE,"E48.2.0.15"),sQuery(id+"F0.wireOp",EDGE,"E48.2.0.16"),sQuery(id+"F0.wireOp",EDGE,"E48.2.0.17"),sQuery(id+"F0.wireOp",EDGE,"E48.2.0.18"),sQuery(id+"F0.wireOp",EDGE,"E48.2.0.19"),sQuery(id+"F0.wireOp",EDGE,"E48.2.0.20"),sQuery(id+"F0.wireOp",EDGE,"E48.2.0.21"),sQuery(id+"F0.wireOp",EDGE,"E49.1.0.0"),sQuery(id+"F0.wireOp",EDGE,"E49.1.0.1"),sQuery(id+"F0.wireOp",EDGE,"E49.1.0.2"),sQuery(id+"F0.wireOp",EDGE,"E49.1.0.4"),sQuery(id+"F0.wireOp",EDGE,"E49.1.0.6"),sQuery(id+"F0.wireOp",EDGE,"E49.1.0.7"),sQuery(id+"F0.wireOp",EDGE,"E49.1.0.9"),sQuery(id+"F0.wireOp",EDGE,"E49.1.0.10"),sQuery(id+"F0.wireOp",EDGE,"E49.1.0.12"),sQuery(id+"F0.wireOp",EDGE,"E49.1.0.14"),sQuery(id+"F0.wireOp",EDGE,"E49.1.0.16"),sQuery(id+"F0.wireOp",EDGE,"E49.1.0.18"),sQuery(id+"F0.wireOp",EDGE,"E49.1.0.19"),sQuery(id+"F0.wireOp",EDGE,"E49.1.0.20"),sQuery(id+"F0.wireOp",EDGE,"E49.1.0.26"),sQuery(id+"F0.wireOp",EDGE,"E49.1.0.28"),sQuery(id+"F0.wireOp",EDGE,"E49.1.0.29"),sQuery(id+"F0.wireOp",EDGE,"E49.1.0.30"),sQuery(id+"F0.wireOp",EDGE,"E49.2.0.0"),sQuery(id+"F0.wireOp",EDGE,"E49.2.0.1"),sQuery(id+"F0.wireOp",EDGE,"E49.2.0.2"),sQuery(id+"F0.wireOp",EDGE,"E49.2.0.4"),sQuery(id+"F0.wireOp",EDGE,"E49.2.0.6"),sQuery(id+"F0.wireOp",EDGE,"E49.2.0.7"),sQuery(id+"F0.wireOp",EDGE,"E49.2.0.9"),sQuery(id+"F0.wireOp",EDGE,"E49.2.0.10"),sQuery(id+"F0.wireOp",EDGE,"E49.2.0.12"),sQuery(id+"F0.wireOp",EDGE,"E49.2.0.14"),sQuery(id+"F0.wireOp",EDGE,"E49.2.0.16"),sQuery(id+"F0.wireOp",EDGE,"E49.2.0.18"),sQuery(id+"F0.wireOp",EDGE,"E49.2.0.19"),sQuery(id+"F0.wireOp",EDGE,"E49.2.0.20"),sQuery(id+"F0.wireOp",EDGE,"E49.2.0.26"),sQuery(id+"F0.wireOp",EDGE,"E49.2.0.28"),sQuery(id+"F0.wireOp",EDGE,"E49.2.0.29"),sQuery(id+"F0.wireOp",EDGE,"E49.2.0.30")])],"isStart":false});
            extrude(context, id + "F2", {"entities" : qUnion([Q0]), "operationType" : NewBodyOperationType.ADD, "depth" : 5 * mm});
        }
        {
            var Q0;
            Q0=makeQuery(id+"F2.opExtrude","CAP_FACE",FACE,{"disambiguationData":[OSD([sQuery(id+"F0.wireOp",EDGE,"E0.bottom"),sQuery(id+"F0.wireOp",EDGE,"E0.top"),sQuery(id+"F0.wireOp",EDGE,"E0.left"),sQuery(id+"F0.wireOp",EDGE,"E0.right"),sQuery(id+"F0.wireOp",EDGE,"E5"),sQuery(id+"F0.wireOp",EDGE,"E6"),sQuery(id+"F0.wireOp",EDGE,"E7"),sQuery(id+"F0.wireOp",EDGE,"E10"),sQuery(id+"F0.wireOp",EDGE,"E11"),sQuery(id+"F0.wireOp",EDGE,"E12"),sQuery(id+"F0.wireOp",EDGE,"E13"),sQuery(id+"F0.wireOp",EDGE,"E14"),sQuery(id+"F0.wireOp",EDGE,"E15"),sQuery(id+"F0.wireOp",EDGE,"E16"),sQuery(id+"F0.wireOp",EDGE,"E17.bottom"),sQuery(id+"F0.wireOp",EDGE,"E17.top"),sQuery(id+"F0.wireOp",EDGE,"E17.left"),sQuery(id+"F0.wireOp",EDGE,"E17.right"),sQuery(id+"F0.wireOp",EDGE,"E18"),sQuery(id+"F0.wireOp",EDGE,"E19"),sQuery(id+"F0.wireOp",EDGE,"E21.bottom"),sQuery(id+"F0.wireOp",EDGE,"E21.top"),sQuery(id+"F0.wireOp",EDGE,"E21.left"),sQuery(id+"F0.wireOp",EDGE,"E21.right"),sQuery(id+"F0.wireOp",EDGE,"E23.bottom"),sQuery(id+"F0.wireOp",EDGE,"E23.top"),sQuery(id+"F0.wireOp",EDGE,"E24.left"),sQuery(id+"F0.wireOp",EDGE,"E24.right"),sQuery(id+"F0.wireOp",EDGE,"E25.left"),sQuery(id+"F0.wireOp",EDGE,"E25.right"),sQuery(id+"F0.wireOp",EDGE,"E26.trimOffspring"),sQuery(id+"F0.wireOp",EDGE,"E27.trimOffspring"),sQuery(id+"F0.wireOp",EDGE,"E28.trimOffspring"),sQuery(id+"F0.wireOp",EDGE,"E29.trimOffspring"),sQuery(id+"F0.wireOp",EDGE,"E30.trimOffspring"),sQuery(id+"F0.wireOp",EDGE,"E31.trimOffspring"),sQuery(id+"F0.wireOp",EDGE,"E32.trimOffspring"),sQuery(id+"F0.wireOp",EDGE,"E33.trimOffspring"),sQuery(id+"F0.wireOp",EDGE,"E22.bottom"),sQuery(id+"F0.wireOp",EDGE,"E22.top"),sQuery(id+"F0.wireOp",EDGE,"E22.left"),sQuery(id+"F0.wireOp",EDGE,"E22.right"),sQuery(id+"F0.wireOp",EDGE,"E35.bottom"),sQuery(id+"F0.wireOp",EDGE,"E35.top"),sQuery(id+"F0.wireOp",EDGE,"E36.left"),sQuery(id+"F0.wireOp",EDGE,"E36.right"),sQuery(id+"F0.wireOp",EDGE,"E37.left"),sQuery(id+"F0.wireOp",EDGE,"E37.right"),sQuery(id+"F0.wireOp",EDGE,"E38.trimOffspring"),sQuery(id+"F0.wireOp",EDGE,"E39.trimOffspring"),sQuery(id+"F0.wireOp",EDGE,"E40.trimOffspring"),sQuery(id+"F0.wireOp",EDGE,"E41.trimOffspring"),sQuery(id+"F0.wireOp",EDGE,"E42.trimOffspring"),sQuery(id+"F0.wireOp",EDGE,"E43.trimOffspring"),sQuery(id+"F0.wireOp",EDGE,"E44.trimOffspring"),sQuery(id+"F0.wireOp",EDGE,"E45.trimOffspring"),sQuery(id+"F0.wireOp",EDGE,"E46.bottom"),sQuery(id+"F0.wireOp",EDGE,"E46.top"),sQuery(id+"F0.wireOp",EDGE,"E46.left"),sQuery(id+"F0.wireOp",EDGE,"E46.right"),sQuery(id+"F0.wireOp",EDGE,"E47.bottom"),sQuery(id+"F0.wireOp",EDGE,"E47.top"),sQuery(id+"F0.wireOp",EDGE,"E47.left"),sQuery(id+"F0.wireOp",EDGE,"E47.right"),sQuery(id+"F0.wireOp",EDGE,"E48.1.0.0"),sQuery(id+"F0.wireOp",EDGE,"E48.1.0.2"),sQuery(id+"F0.wireOp",EDGE,"E48.1.0.3"),sQuery(id+"F0.wireOp",EDGE,"E48.1.0.5"),sQuery(id+"F0.wireOp",EDGE,"E48.1.0.6"),sQuery(id+"F0.wireOp",EDGE,"E48.1.0.7"),sQuery(id+"F0.wireOp",EDGE,"E48.1.0.8"),sQuery(id+"F0.wireOp",EDGE,"E48.1.0.9"),sQuery(id+"F0.wireOp",EDGE,"E48.1.0.12"),sQuery(id+"F0.wireOp",EDGE,"E48.1.0.13"),sQuery(id+"F0.wireOp",EDGE,"E48.1.0.14"),sQuery(id+"F0.wireOp",EDGE,"E48.1.0.15"),sQuery(id+"F0.wireOp",EDGE,"E48.1.0.16"),sQuery(id+"F0.wireOp",EDGE,"E48.1.0.17"),sQuery(id+"F0.wireOp",EDGE,"E48.1.0.18"),sQuery(id+"F0.wireOp",EDGE,"E48.1.0.19"),sQuery(id+"F0.wireOp",EDGE,"E48.1.0.20"),sQuery(id+"F0.wireOp",EDGE,"E48.1.0.21"),sQuery(id+"F0.wireOp",EDGE,"E48.2.0.0"),sQuery(id+"F0.wireOp",EDGE,"E48.2.0.2"),sQuery(id+"F0.wireOp",EDGE,"E48.2.0.3"),sQuery(id+"F0.wireOp",EDGE,"E48.2.0.5"),sQuery(id+"F0.wireOp",EDGE,"E48.2.0.6"),sQuery(id+"F0.wireOp",EDGE,"E48.2.0.7"),sQuery(id+"F0.wireOp",EDGE,"E48.2.0.8"),sQuery(id+"F0.wireOp",EDGE,"E48.2.0.9"),sQuery(id+"F0.wireOp",EDGE,"E48.2.0.12"),sQuery(id+"F0.wireOp",EDGE,"E48.2.0.13"),sQuery(id+"F0.wireOp",EDGE,"E48.2.0.14"),sQuery(id+"F0.wireOp",EDGE,"E48.2.0.15"),sQuery(id+"F0.wireOp",EDGE,"E48.2.0.16"),sQuery(id+"F0.wireOp",EDGE,"E48.2.0.17"),sQuery(id+"F0.wireOp",EDGE,"E48.2.0.18"),sQuery(id+"F0.wireOp",EDGE,"E48.2.0.19"),sQuery(id+"F0.wireOp",EDGE,"E48.2.0.20"),sQuery(id+"F0.wireOp",EDGE,"E48.2.0.21"),sQuery(id+"F0.wireOp",EDGE,"E49.1.0.0"),sQuery(id+"F0.wireOp",EDGE,"E49.1.0.1"),sQuery(id+"F0.wireOp",EDGE,"E49.1.0.2"),sQuery(id+"F0.wireOp",EDGE,"E49.1.0.4"),sQuery(id+"F0.wireOp",EDGE,"E49.1.0.6"),sQuery(id+"F0.wireOp",EDGE,"E49.1.0.7"),sQuery(id+"F0.wireOp",EDGE,"E49.1.0.9"),sQuery(id+"F0.wireOp",EDGE,"E49.1.0.10"),sQuery(id+"F0.wireOp",EDGE,"E49.1.0.12"),sQuery(id+"F0.wireOp",EDGE,"E49.1.0.14"),sQuery(id+"F0.wireOp",EDGE,"E49.1.0.16"),sQuery(id+"F0.wireOp",EDGE,"E49.1.0.18"),sQuery(id+"F0.wireOp",EDGE,"E49.1.0.19"),sQuery(id+"F0.wireOp",EDGE,"E49.1.0.20"),sQuery(id+"F0.wireOp",EDGE,"E49.1.0.26"),sQuery(id+"F0.wireOp",EDGE,"E49.1.0.28"),sQuery(id+"F0.wireOp",EDGE,"E49.1.0.29"),sQuery(id+"F0.wireOp",EDGE,"E49.1.0.30"),sQuery(id+"F0.wireOp",EDGE,"E49.2.0.0"),sQuery(id+"F0.wireOp",EDGE,"E49.2.0.1"),sQuery(id+"F0.wireOp",EDGE,"E49.2.0.2"),sQuery(id+"F0.wireOp",EDGE,"E49.2.0.4"),sQuery(id+"F0.wireOp",EDGE,"E49.2.0.6"),sQuery(id+"F0.wireOp",EDGE,"E49.2.0.7"),sQuery(id+"F0.wireOp",EDGE,"E49.2.0.9"),sQuery(id+"F0.wireOp",EDGE,"E49.2.0.10"),sQuery(id+"F0.wireOp",EDGE,"E49.2.0.12"),sQuery(id+"F0.wireOp",EDGE,"E49.2.0.14"),sQuery(id+"F0.wireOp",EDGE,"E49.2.0.16"),sQuery(id+"F0.wireOp",EDGE,"E49.2.0.18"),sQuery(id+"F0.wireOp",EDGE,"E49.2.0.19"),sQuery(id+"F0.wireOp",EDGE,"E49.2.0.20"),sQuery(id+"F0.wireOp",EDGE,"E49.2.0.26"),sQuery(id+"F0.wireOp",EDGE,"E49.2.0.28"),sQuery(id+"F0.wireOp",EDGE,"E49.2.0.29"),sQuery(id+"F0.wireOp",EDGE,"E49.2.0.30")])],"isStart":false});
            var sketch = newSketch(context, id + "F3", { "sketchPlane" : qUnion([Q0])});
            skPoint(sketch, "E52.0", {"position": v(-111.5, 3.96) * mm});
            skLineSegment(sketch, "E53.bottom", {"start": v(-102.5, -5.04) * mm, "end": v(-120.5, -5.04) * mm});
            skLineSegment(sketch, "E53.top", {"start": v(-102.5, 12.96) * mm, "end": v(-120.5, 12.96) * mm});
            skLineSegment(sketch, "E53.left", {"start": v(-102.5, -5.04) * mm, "end": v(-102.5, 12.96) * mm});
            skLineSegment(sketch, "E53.right", {"start": v(-120.5, -5.04) * mm, "end": v(-120.5, 12.96) * mm});
            skPoint(sketch, "E54.0", {"position": v(-111.5, -21.04) * mm});
            skLineSegment(sketch, "E55.bottom", {"start": v(-102.5, -30.04) * mm, "end": v(-120.5, -30.04) * mm});
            skLineSegment(sketch, "E55.top", {"start": v(-102.5, -12.04) * mm, "end": v(-120.5, -12.04) * mm});
            skLineSegment(sketch, "E55.left", {"start": v(-102.5, -30.04) * mm, "end": v(-102.5, -12.04) * mm});
            skLineSegment(sketch, "E55.right", {"start": v(-120.5, -30.04) * mm, "end": v(-120.5, -12.04) * mm});
            skLineSegment(sketch, "E56.1.0.0", {"start": v(-76.5, -5.04) * mm, "end": v(-94.5, -5.04) * mm});
            skLineSegment(sketch, "E56.1.0.1", {"start": v(-76.5, -12.04) * mm, "end": v(-94.5, -12.04) * mm});
            skLineSegment(sketch, "E56.1.0.2", {"start": v(-94.5, -5.04) * mm, "end": v(-94.5, 12.96) * mm});
            skPoint(sketch, "E56.1.0.3", {"position": v(-85.5, 3.96) * mm});
            skLineSegment(sketch, "E56.1.0.4", {"start": v(-76.5, -30.04) * mm, "end": v(-76.5, -12.04) * mm});
            skLineSegment(sketch, "E56.1.0.5", {"start": v(-76.5, -30.04) * mm, "end": v(-94.5, -30.04) * mm});
            skPoint(sketch, "E56.1.0.6", {"position": v(-85.5, -21.04) * mm});
            skLineSegment(sketch, "E56.1.0.7", {"start": v(-76.5, -5.04) * mm, "end": v(-76.5, 12.96) * mm});
            skLineSegment(sketch, "E56.1.0.8", {"start": v(-76.5, 12.96) * mm, "end": v(-94.5, 12.96) * mm});
            skLineSegment(sketch, "E56.1.0.9", {"start": v(-94.5, -30.04) * mm, "end": v(-94.5, -12.04) * mm});
            skPoint(sketch, "E56.1.0.10", {"position": v(-85.5, 3.96) * mm});
            skPoint(sketch, "E56.1.0.11", {"position": v(-85.5, -21.04) * mm});
            skLineSegment(sketch, "E56.2.0.0", {"start": v(-50.5, -5.04) * mm, "end": v(-68.5, -5.04) * mm});
            skLineSegment(sketch, "E56.2.0.1", {"start": v(-50.5, -12.04) * mm, "end": v(-68.5, -12.04) * mm});
            skLineSegment(sketch, "E56.2.0.2", {"start": v(-68.5, -5.04) * mm, "end": v(-68.5, 12.96) * mm});
            skPoint(sketch, "E56.2.0.3", {"position": v(-59.5, 3.96) * mm});
            skLineSegment(sketch, "E56.2.0.4", {"start": v(-50.5, -30.04) * mm, "end": v(-50.5, -12.04) * mm});
            skLineSegment(sketch, "E56.2.0.5", {"start": v(-50.5, -30.04) * mm, "end": v(-68.5, -30.04) * mm});
            skPoint(sketch, "E56.2.0.6", {"position": v(-59.5, -21.04) * mm});
            skLineSegment(sketch, "E56.2.0.7", {"start": v(-50.5, -5.04) * mm, "end": v(-50.5, 12.96) * mm});
            skLineSegment(sketch, "E56.2.0.8", {"start": v(-50.5, 12.96) * mm, "end": v(-68.5, 12.96) * mm});
            skLineSegment(sketch, "E56.2.0.9", {"start": v(-68.5, -30.04) * mm, "end": v(-68.5, -12.04) * mm});
            skPoint(sketch, "E56.2.0.10", {"position": v(-59.5, 3.96) * mm});
            skPoint(sketch, "E56.2.0.11", {"position": v(-59.5, -21.04) * mm});
            skLineSegment(sketch, "E56.direction1", {"start": v(-120.5, -30.04) * mm, "end": v(-94.5, -30.04) * mm, "construction": true});
            skSolve(sketch);
        }
        {
            var Q0;
            Q0=qSketchRegion(id+"F3",true);
            extrude(context, id + "F4", {"entities" : qUnion([Q0]), "operationType" : NewBodyOperationType.REMOVE, "oppositeDirection" : true, "depth" : 5 * mm});
        }
        {
            var Q0;
            Q0=makeQuery(id+"F2.opExtrude","CAP_FACE",FACE,{"disambiguationData":[OSD([sQuery(id+"F0.wireOp",EDGE,"E0.bottom"),sQuery(id+"F0.wireOp",EDGE,"E0.top"),sQuery(id+"F0.wireOp",EDGE,"E0.left"),sQuery(id+"F0.wireOp",EDGE,"E0.right"),sQuery(id+"F0.wireOp",EDGE,"E5"),sQuery(id+"F0.wireOp",EDGE,"E6"),sQuery(id+"F0.wireOp",EDGE,"E7"),sQuery(id+"F0.wireOp",EDGE,"E10"),sQuery(id+"F0.wireOp",EDGE,"E11"),sQuery(id+"F0.wireOp",EDGE,"E12"),sQuery(id+"F0.wireOp",EDGE,"E13"),sQuery(id+"F0.wireOp",EDGE,"E14"),sQuery(id+"F0.wireOp",EDGE,"E15"),sQuery(id+"F0.wireOp",EDGE,"E16"),sQuery(id+"F0.wireOp",EDGE,"E17.bottom"),sQuery(id+"F0.wireOp",EDGE,"E17.top"),sQuery(id+"F0.wireOp",EDGE,"E17.left"),sQuery(id+"F0.wireOp",EDGE,"E17.right"),sQuery(id+"F0.wireOp",EDGE,"E18"),sQuery(id+"F0.wireOp",EDGE,"E19"),sQuery(id+"F0.wireOp",EDGE,"E21.bottom"),sQuery(id+"F0.wireOp",EDGE,"E21.top"),sQuery(id+"F0.wireOp",EDGE,"E21.left"),sQuery(id+"F0.wireOp",EDGE,"E21.right"),sQuery(id+"F0.wireOp",EDGE,"E23.bottom"),sQuery(id+"F0.wireOp",EDGE,"E23.top"),sQuery(id+"F0.wireOp",EDGE,"E24.left"),sQuery(id+"F0.wireOp",EDGE,"E24.right"),sQuery(id+"F0.wireOp",EDGE,"E25.left"),sQuery(id+"F0.wireOp",EDGE,"E25.right"),sQuery(id+"F0.wireOp",EDGE,"E26.trimOffspring"),sQuery(id+"F0.wireOp",EDGE,"E27.trimOffspring"),sQuery(id+"F0.wireOp",EDGE,"E28.trimOffspring"),sQuery(id+"F0.wireOp",EDGE,"E29.trimOffspring"),sQuery(id+"F0.wireOp",EDGE,"E30.trimOffspring"),sQuery(id+"F0.wireOp",EDGE,"E31.trimOffspring"),sQuery(id+"F0.wireOp",EDGE,"E32.trimOffspring"),sQuery(id+"F0.wireOp",EDGE,"E33.trimOffspring"),sQuery(id+"F0.wireOp",EDGE,"E22.bottom"),sQuery(id+"F0.wireOp",EDGE,"E22.top"),sQuery(id+"F0.wireOp",EDGE,"E22.left"),sQuery(id+"F0.wireOp",EDGE,"E22.right"),sQuery(id+"F0.wireOp",EDGE,"E35.bottom"),sQuery(id+"F0.wireOp",EDGE,"E35.top"),sQuery(id+"F0.wireOp",EDGE,"E36.left"),sQuery(id+"F0.wireOp",EDGE,"E36.right"),sQuery(id+"F0.wireOp",EDGE,"E37.left"),sQuery(id+"F0.wireOp",EDGE,"E37.right"),sQuery(id+"F0.wireOp",EDGE,"E38.trimOffspring"),sQuery(id+"F0.wireOp",EDGE,"E39.trimOffspring"),sQuery(id+"F0.wireOp",EDGE,"E40.trimOffspring"),sQuery(id+"F0.wireOp",EDGE,"E41.trimOffspring"),sQuery(id+"F0.wireOp",EDGE,"E42.trimOffspring"),sQuery(id+"F0.wireOp",EDGE,"E43.trimOffspring"),sQuery(id+"F0.wireOp",EDGE,"E44.trimOffspring"),sQuery(id+"F0.wireOp",EDGE,"E45.trimOffspring"),sQuery(id+"F0.wireOp",EDGE,"E46.bottom"),sQuery(id+"F0.wireOp",EDGE,"E46.top"),sQuery(id+"F0.wireOp",EDGE,"E46.left"),sQuery(id+"F0.wireOp",EDGE,"E46.right"),sQuery(id+"F0.wireOp",EDGE,"E47.bottom"),sQuery(id+"F0.wireOp",EDGE,"E47.top"),sQuery(id+"F0.wireOp",EDGE,"E47.left"),sQuery(id+"F0.wireOp",EDGE,"E47.right"),sQuery(id+"F0.wireOp",EDGE,"E48.1.0.0"),sQuery(id+"F0.wireOp",EDGE,"E48.1.0.2"),sQuery(id+"F0.wireOp",EDGE,"E48.1.0.3"),sQuery(id+"F0.wireOp",EDGE,"E48.1.0.5"),sQuery(id+"F0.wireOp",EDGE,"E48.1.0.6"),sQuery(id+"F0.wireOp",EDGE,"E48.1.0.7"),sQuery(id+"F0.wireOp",EDGE,"E48.1.0.8"),sQuery(id+"F0.wireOp",EDGE,"E48.1.0.9"),sQuery(id+"F0.wireOp",EDGE,"E48.1.0.12"),sQuery(id+"F0.wireOp",EDGE,"E48.1.0.13"),sQuery(id+"F0.wireOp",EDGE,"E48.1.0.14"),sQuery(id+"F0.wireOp",EDGE,"E48.1.0.15"),sQuery(id+"F0.wireOp",EDGE,"E48.1.0.16"),sQuery(id+"F0.wireOp",EDGE,"E48.1.0.17"),sQuery(id+"F0.wireOp",EDGE,"E48.1.0.18"),sQuery(id+"F0.wireOp",EDGE,"E48.1.0.19"),sQuery(id+"F0.wireOp",EDGE,"E48.1.0.20"),sQuery(id+"F0.wireOp",EDGE,"E48.1.0.21"),sQuery(id+"F0.wireOp",EDGE,"E48.2.0.0"),sQuery(id+"F0.wireOp",EDGE,"E48.2.0.2"),sQuery(id+"F0.wireOp",EDGE,"E48.2.0.3"),sQuery(id+"F0.wireOp",EDGE,"E48.2.0.5"),sQuery(id+"F0.wireOp",EDGE,"E48.2.0.6"),sQuery(id+"F0.wireOp",EDGE,"E48.2.0.7"),sQuery(id+"F0.wireOp",EDGE,"E48.2.0.8"),sQuery(id+"F0.wireOp",EDGE,"E48.2.0.9"),sQuery(id+"F0.wireOp",EDGE,"E48.2.0.12"),sQuery(id+"F0.wireOp",EDGE,"E48.2.0.13"),sQuery(id+"F0.wireOp",EDGE,"E48.2.0.14"),sQuery(id+"F0.wireOp",EDGE,"E48.2.0.15"),sQuery(id+"F0.wireOp",EDGE,"E48.2.0.16"),sQuery(id+"F0.wireOp",EDGE,"E48.2.0.17"),sQuery(id+"F0.wireOp",EDGE,"E48.2.0.18"),sQuery(id+"F0.wireOp",EDGE,"E48.2.0.19"),sQuery(id+"F0.wireOp",EDGE,"E48.2.0.20"),sQuery(id+"F0.wireOp",EDGE,"E48.2.0.21"),sQuery(id+"F0.wireOp",EDGE,"E49.1.0.0"),sQuery(id+"F0.wireOp",EDGE,"E49.1.0.1"),sQuery(id+"F0.wireOp",EDGE,"E49.1.0.2"),sQuery(id+"F0.wireOp",EDGE,"E49.1.0.4"),sQuery(id+"F0.wireOp",EDGE,"E49.1.0.6"),sQuery(id+"F0.wireOp",EDGE,"E49.1.0.7"),sQuery(id+"F0.wireOp",EDGE,"E49.1.0.9"),sQuery(id+"F0.wireOp",EDGE,"E49.1.0.10"),sQuery(id+"F0.wireOp",EDGE,"E49.1.0.12"),sQuery(id+"F0.wireOp",EDGE,"E49.1.0.14"),sQuery(id+"F0.wireOp",EDGE,"E49.1.0.16"),sQuery(id+"F0.wireOp",EDGE,"E49.1.0.18"),sQuery(id+"F0.wireOp",EDGE,"E49.1.0.19"),sQuery(id+"F0.wireOp",EDGE,"E49.1.0.20"),sQuery(id+"F0.wireOp",EDGE,"E49.1.0.26"),sQuery(id+"F0.wireOp",EDGE,"E49.1.0.28"),sQuery(id+"F0.wireOp",EDGE,"E49.1.0.29"),sQuery(id+"F0.wireOp",EDGE,"E49.1.0.30"),sQuery(id+"F0.wireOp",EDGE,"E49.2.0.0"),sQuery(id+"F0.wireOp",EDGE,"E49.2.0.1"),sQuery(id+"F0.wireOp",EDGE,"E49.2.0.2"),sQuery(id+"F0.wireOp",EDGE,"E49.2.0.4"),sQuery(id+"F0.wireOp",EDGE,"E49.2.0.6"),sQuery(id+"F0.wireOp",EDGE,"E49.2.0.7"),sQuery(id+"F0.wireOp",EDGE,"E49.2.0.9"),sQuery(id+"F0.wireOp",EDGE,"E49.2.0.10"),sQuery(id+"F0.wireOp",EDGE,"E49.2.0.12"),sQuery(id+"F0.wireOp",EDGE,"E49.2.0.14"),sQuery(id+"F0.wireOp",EDGE,"E49.2.0.16"),sQuery(id+"F0.wireOp",EDGE,"E49.2.0.18"),sQuery(id+"F0.wireOp",EDGE,"E49.2.0.19"),sQuery(id+"F0.wireOp",EDGE,"E49.2.0.20"),sQuery(id+"F0.wireOp",EDGE,"E49.2.0.26"),sQuery(id+"F0.wireOp",EDGE,"E49.2.0.28"),sQuery(id+"F0.wireOp",EDGE,"E49.2.0.29"),sQuery(id+"F0.wireOp",EDGE,"E49.2.0.30")])],"isStart":false});
            var sketch = newSketch(context, id + "F5", { "sketchPlane" : qUnion([Q0])});
            skPoint(sketch, "E57.0", {"position": v(-111.5, 3.96) * mm});
            skPoint(sketch, "E57.1", {"position": v(-111.5, -21.04) * mm});
            skLineSegment(sketch, "E58.bottom", {"start": v(-122.5, 8.96) * mm, "end": v(-120.5, 8.96) * mm});
            skLineSegment(sketch, "E58.top", {"start": v(-122.5, -1.04) * mm, "end": v(-120.5, -1.04) * mm});
            skLineSegment(sketch, "E58.left", {"start": v(-122.5, 8.96) * mm, "end": v(-122.5, -1.04) * mm});
            skLineSegment(sketch, "E58.right", {"start": v(-120.5, 8.96) * mm, "end": v(-120.5, -1.04) * mm});
            skPoint(sketch, "E59", {"position": v(-121.5, 3.96) * mm});
            skPoint(sketch, "E59.positionSnap0", {"position": v(-121.5, 8.96) * mm});
            skPoint(sketch, "E59.positionSnap1", {"position": v(-122.5, 3.96) * mm});
            skPoint(sketch, "E60.firstSnap0", {"position": v(-102.5, 3.96) * mm});
            skLineSegment(sketch, "E60.bottom", {"start": v(-102.5, 8.96) * mm, "end": v(-100.5, 8.96) * mm});
            skLineSegment(sketch, "E60.top", {"start": v(-102.5, -1.04) * mm, "end": v(-100.5, -1.04) * mm});
            skLineSegment(sketch, "E60.left", {"start": v(-102.5, 8.96) * mm, "end": v(-102.5, -1.04) * mm});
            skLineSegment(sketch, "E60.right", {"start": v(-100.5, 8.96) * mm, "end": v(-100.5, -1.04) * mm});
            skLineSegment(sketch, "E61.1.0.0", {"start": v(-76.5, 8.96) * mm, "end": v(-76.5, -1.04) * mm});
            skLineSegment(sketch, "E61.1.0.1", {"start": v(-74.5, 8.96) * mm, "end": v(-74.5, -1.04) * mm});
            skPoint(sketch, "E61.1.0.2", {"position": v(-85.5, 3.96) * mm});
            skPoint(sketch, "E61.1.0.3", {"position": v(-96.5, 3.96) * mm});
            skPoint(sketch, "E61.1.0.4", {"position": v(-95.5, 3.96) * mm});
            skLineSegment(sketch, "E61.1.0.5", {"start": v(-96.5, -1.04) * mm, "end": v(-94.5, -1.04) * mm});
            skLineSegment(sketch, "E61.1.0.6", {"start": v(-76.5, 8.96) * mm, "end": v(-74.5, 8.96) * mm});
            skPoint(sketch, "E61.1.0.7", {"position": v(-76.5, 3.96) * mm});
            skPoint(sketch, "E61.1.0.8", {"position": v(-95.5, 8.96) * mm});
            skLineSegment(sketch, "E61.1.0.9", {"start": v(-94.5, 8.96) * mm, "end": v(-94.5, -1.04) * mm});
            skLineSegment(sketch, "E61.1.0.10", {"start": v(-76.5, -1.04) * mm, "end": v(-74.5, -1.04) * mm});
            skLineSegment(sketch, "E61.1.0.11", {"start": v(-96.5, 8.96) * mm, "end": v(-96.5, -1.04) * mm});
            skLineSegment(sketch, "E61.1.0.12", {"start": v(-96.5, 8.96) * mm, "end": v(-94.5, 8.96) * mm});
            skLineSegment(sketch, "E61.2.0.0", {"start": v(-50.5, 8.96) * mm, "end": v(-50.5, -1.04) * mm});
            skLineSegment(sketch, "E61.2.0.1", {"start": v(-48.5, 8.96) * mm, "end": v(-48.5, -1.04) * mm});
            skPoint(sketch, "E61.2.0.2", {"position": v(-59.5, 3.96) * mm});
            skPoint(sketch, "E61.2.0.3", {"position": v(-70.5, 3.96) * mm});
            skPoint(sketch, "E61.2.0.4", {"position": v(-69.5, 3.96) * mm});
            skLineSegment(sketch, "E61.2.0.5", {"start": v(-70.5, -1.04) * mm, "end": v(-68.5, -1.04) * mm});
            skLineSegment(sketch, "E61.2.0.6", {"start": v(-50.5, 8.96) * mm, "end": v(-48.5, 8.96) * mm});
            skPoint(sketch, "E61.2.0.7", {"position": v(-50.5, 3.96) * mm});
            skPoint(sketch, "E61.2.0.8", {"position": v(-69.5, 8.96) * mm});
            skLineSegment(sketch, "E61.2.0.9", {"start": v(-68.5, 8.96) * mm, "end": v(-68.5, -1.04) * mm});
            skLineSegment(sketch, "E61.2.0.10", {"start": v(-50.5, -1.04) * mm, "end": v(-48.5, -1.04) * mm});
            skLineSegment(sketch, "E61.2.0.11", {"start": v(-70.5, 8.96) * mm, "end": v(-70.5, -1.04) * mm});
            skLineSegment(sketch, "E61.2.0.12", {"start": v(-70.5, 8.96) * mm, "end": v(-68.5, 8.96) * mm});
            skLineSegment(sketch, "E61.direction1", {"start": v(-122.5, -1.04) * mm, "end": v(-96.5, -1.04) * mm, "construction": true});
            skLineSegment(sketch, "E62.bottom", {"start": v(-120.5, -16.04) * mm, "end": v(-122.5, -16.04) * mm});
            skLineSegment(sketch, "E62.top", {"start": v(-120.5, -26.04) * mm, "end": v(-122.5, -26.04) * mm});
            skLineSegment(sketch, "E62.left", {"start": v(-120.5, -16.04) * mm, "end": v(-120.5, -26.04) * mm});
            skLineSegment(sketch, "E62.right", {"start": v(-122.5, -16.04) * mm, "end": v(-122.5, -26.04) * mm});
            skLineSegment(sketch, "E63.bottom", {"start": v(-102.5, -16.04) * mm, "end": v(-100.5, -16.04) * mm});
            skLineSegment(sketch, "E63.top", {"start": v(-102.5, -26.04) * mm, "end": v(-100.5, -26.04) * mm});
            skLineSegment(sketch, "E63.left", {"start": v(-102.5, -16.04) * mm, "end": v(-102.5, -26.04) * mm});
            skLineSegment(sketch, "E63.right", {"start": v(-100.5, -16.04) * mm, "end": v(-100.5, -26.04) * mm});
            skLineSegment(sketch, "E64.1.0.0", {"start": v(-94.5, -16.04) * mm, "end": v(-94.5, -26.04) * mm});
            skPoint(sketch, "E64.1.0.1", {"position": v(-85.5, -21.04) * mm});
            skLineSegment(sketch, "E64.1.0.2", {"start": v(-76.5, -26.04) * mm, "end": v(-74.5, -26.04) * mm});
            skLineSegment(sketch, "E64.1.0.3", {"start": v(-74.5, -16.04) * mm, "end": v(-74.5, -26.04) * mm});
            skLineSegment(sketch, "E64.1.0.4", {"start": v(-94.5, -16.04) * mm, "end": v(-96.5, -16.04) * mm});
            skLineSegment(sketch, "E64.1.0.5", {"start": v(-76.5, -16.04) * mm, "end": v(-76.5, -26.04) * mm});
            skLineSegment(sketch, "E64.1.0.6", {"start": v(-94.5, -26.04) * mm, "end": v(-96.5, -26.04) * mm});
            skLineSegment(sketch, "E64.1.0.7", {"start": v(-76.5, -16.04) * mm, "end": v(-74.5, -16.04) * mm});
            skLineSegment(sketch, "E64.1.0.8", {"start": v(-96.5, -16.04) * mm, "end": v(-96.5, -26.04) * mm});
            skLineSegment(sketch, "E64.2.0.0", {"start": v(-68.5, -16.04) * mm, "end": v(-68.5, -26.04) * mm});
            skPoint(sketch, "E64.2.0.1", {"position": v(-59.5, -21.04) * mm});
            skLineSegment(sketch, "E64.2.0.2", {"start": v(-50.5, -26.04) * mm, "end": v(-48.5, -26.04) * mm});
            skLineSegment(sketch, "E64.2.0.3", {"start": v(-48.5, -16.04) * mm, "end": v(-48.5, -26.04) * mm});
            skLineSegment(sketch, "E64.2.0.4", {"start": v(-68.5, -16.04) * mm, "end": v(-70.5, -16.04) * mm});
            skLineSegment(sketch, "E64.2.0.5", {"start": v(-50.5, -16.04) * mm, "end": v(-50.5, -26.04) * mm});
            skLineSegment(sketch, "E64.2.0.6", {"start": v(-68.5, -26.04) * mm, "end": v(-70.5, -26.04) * mm});
            skLineSegment(sketch, "E64.2.0.7", {"start": v(-50.5, -16.04) * mm, "end": v(-48.5, -16.04) * mm});
            skLineSegment(sketch, "E64.2.0.8", {"start": v(-70.5, -16.04) * mm, "end": v(-70.5, -26.04) * mm});
            skLineSegment(sketch, "E64.direction1", {"start": v(-122.5, -26.04) * mm, "end": v(-96.5, -26.04) * mm, "construction": true});
            skPoint(sketch, "E65", {"position": v(-121.5, -21.04) * mm});
            skPoint(sketch, "E65.positionSnap0", {"position": v(-121.5, -16.04) * mm});
            skPoint(sketch, "E65.positionSnap1", {"position": v(-122.5, -21.04) * mm});
            skSolve(sketch);
        }
        {
            var Q0;
            Q0=qSketchRegion(id+"F5",true);
            extrude(context, id + "F6", {"entities" : qUnion([Q0]), "operationType" : NewBodyOperationType.REMOVE, "oppositeDirection" : true, "depth" : 5 * mm});
        }
        {
            var Q0;
            Q0=qCreatedBy(makeId("Top.planeOp"),FACE);
            var sketch = newSketch(context, id + "F7", { "sketchPlane" : qUnion([Q0])});
            skLineSegment(sketch, "E66.bottom", {"start": v(-106.79, 77.03) * mm, "end": v(-126.79, 77.03) * mm});
            skLineSegment(sketch, "E66.top", {"start": v(-106.79, 97.03) * mm, "end": v(-126.79, 97.03) * mm});
            skLineSegment(sketch, "E66.left", {"start": v(-106.79, 77.03) * mm, "end": v(-106.79, 97.03) * mm});
            skLineSegment(sketch, "E66.right", {"start": v(-126.79, 77.03) * mm, "end": v(-126.79, 97.03) * mm});
            skPoint(sketch, "E66.middle", {"position": v(-116.79, 87.03) * mm});
            skLineSegment(sketch, "E67.bottom", {"start": v(-105.79, 82.03) * mm, "end": v(-107.79, 82.03) * mm});
            skLineSegment(sketch, "E67.top", {"start": v(-105.79, 92.03) * mm, "end": v(-107.79, 92.03) * mm});
            skLineSegment(sketch, "E67.left", {"start": v(-105.79, 82.03) * mm, "end": v(-105.79, 92.03) * mm});
            skLineSegment(sketch, "E67.right", {"start": v(-107.79, 82.03) * mm, "end": v(-107.79, 92.03) * mm});
            skPoint(sketch, "E67.middle", {"position": v(-106.79, 87.03) * mm});
            skLineSegment(sketch, "E68.bottom", {"start": v(-125.79, 82.03) * mm, "end": v(-127.79, 82.03) * mm});
            skLineSegment(sketch, "E68.top", {"start": v(-125.79, 92.03) * mm, "end": v(-127.79, 92.03) * mm});
            skLineSegment(sketch, "E68.left", {"start": v(-125.79, 82.03) * mm, "end": v(-125.79, 92.03) * mm});
            skLineSegment(sketch, "E68.right", {"start": v(-127.79, 82.03) * mm, "end": v(-127.79, 92.03) * mm});
            skPoint(sketch, "E68.middle", {"position": v(-126.79, 87.03) * mm});
            skLineSegment(sketch, "E69.bottom", {"start": v(-107.79, 78.03) * mm, "end": v(-125.79, 78.03) * mm});
            skLineSegment(sketch, "E69.top", {"start": v(-107.79, 96.03) * mm, "end": v(-125.79, 96.03) * mm});
            skLineSegment(sketch, "E69.left", {"start": v(-107.79, 78.03) * mm, "end": v(-107.79, 96.03) * mm});
            skLineSegment(sketch, "E69.right", {"start": v(-125.79, 78.03) * mm, "end": v(-125.79, 96.03) * mm});
            skLineSegment(sketch, "E70.bottom", {"start": v(-107.79, 86.53) * mm, "end": v(-125.79, 86.53) * mm});
            skLineSegment(sketch, "E70.top", {"start": v(-107.79, 87.53) * mm, "end": v(-125.79, 87.53) * mm});
            skLineSegment(sketch, "E70.left", {"start": v(-107.79, 86.53) * mm, "end": v(-107.79, 87.53) * mm});
            skLineSegment(sketch, "E70.right", {"start": v(-125.79, 86.53) * mm, "end": v(-125.79, 87.53) * mm});
            skLineSegment(sketch, "E71.bottom", {"start": v(-115.79, 85.78) * mm, "end": v(-117.79, 85.78) * mm, "construction": true});
            skLineSegment(sketch, "E71.top", {"start": v(-115.79, 88.28) * mm, "end": v(-117.79, 88.28) * mm, "construction": true});
            skLineSegment(sketch, "E71.left", {"start": v(-115.79, 85.78) * mm, "end": v(-115.79, 88.28) * mm, "construction": true});
            skLineSegment(sketch, "E71.right", {"start": v(-117.79, 85.78) * mm, "end": v(-117.79, 88.28) * mm, "construction": true});
            skLineSegment(sketch, "E72.bottom", {"start": v(-110.82, 38.4) * mm, "end": v(-132.62, 38.4) * mm});
            skLineSegment(sketch, "E72.top", {"start": v(-110.82, 60.2) * mm, "end": v(-132.62, 60.2) * mm});
            skLineSegment(sketch, "E72.left", {"start": v(-110.82, 38.4) * mm, "end": v(-110.82, 60.2) * mm});
            skLineSegment(sketch, "E72.right", {"start": v(-132.62, 38.4) * mm, "end": v(-132.62, 60.2) * mm});
            skPoint(sketch, "E72.middle", {"position": v(-121.72, 49.3) * mm});
            skLineSegment(sketch, "E73.bottom", {"start": v(-110.82, 44.4) * mm, "end": v(-112.62, 44.4) * mm});
            skLineSegment(sketch, "E73.top", {"start": v(-110.82, 54.2) * mm, "end": v(-112.62, 54.2) * mm});
            skLineSegment(sketch, "E73.left", {"start": v(-110.82, 44.4) * mm, "end": v(-110.82, 54.2) * mm});
            skLineSegment(sketch, "E73.right", {"start": v(-112.62, 44.4) * mm, "end": v(-112.62, 54.2) * mm});
            skPoint(sketch, "E73.middle", {"position": v(-111.72, 49.3) * mm});
            skLineSegment(sketch, "E74.bottom", {"start": v(-130.82, 44.4) * mm, "end": v(-132.62, 44.4) * mm});
            skLineSegment(sketch, "E74.top", {"start": v(-130.82, 54.2) * mm, "end": v(-132.62, 54.2) * mm});
            skLineSegment(sketch, "E74.left", {"start": v(-130.82, 44.4) * mm, "end": v(-130.82, 54.2) * mm});
            skLineSegment(sketch, "E74.right", {"start": v(-132.62, 44.4) * mm, "end": v(-132.62, 54.2) * mm});
            skPoint(sketch, "E74.middle", {"position": v(-131.72, 49.3) * mm});
            skLineSegment(sketch, "E75.bottom", {"start": v(-112.62, 40.2) * mm, "end": v(-130.82, 40.2) * mm});
            skLineSegment(sketch, "E75.top", {"start": v(-112.62, 58.4) * mm, "end": v(-130.82, 58.4) * mm});
            skLineSegment(sketch, "E75.left", {"start": v(-112.62, 40.2) * mm, "end": v(-112.62, 58.4) * mm});
            skLineSegment(sketch, "E75.right", {"start": v(-130.82, 40.2) * mm, "end": v(-130.82, 58.4) * mm});
            skSolve(sketch);
        }
        {
            var Q0;
            {var subQ3=sQuery(id+"F7.wireOp",EDGE,"E70.left");Q0=makeQuery(id+"F7.imprint","IMPRINT",FACE,{"disambiguationData":[TD([[makeQuery(id+"F7.imprint","IMPRINT",EDGE,{"derivedFrom":subQ3}),-1.0]])]});}
            var Q1;
            {var subQ1=sQuery(id+"F7.wireOp",EDGE,"E66.top");Q1=makeQuery(id+"F7.imprint","IMPRINT",FACE,{"disambiguationData":[TD([[makeQuery(id+"F7.imprint","IMPRINT",EDGE,{"derivedFrom":subQ1}),1.0]])]});}
            var Q2;
            {var subQ6=sQuery(id+"F7.wireOp",EDGE,"E66.bottom");Q2=makeQuery(id+"F7.imprint","IMPRINT",FACE,{"disambiguationData":[TD([[makeQuery(id+"F7.imprint","IMPRINT",EDGE,{"derivedFrom":subQ6}),-1.0]])]});}
            var Q3;
            {var subQ3=sQuery(id+"F7.wireOp",EDGE,"E70.right");Q3=makeQuery(id+"F7.imprint","IMPRINT",FACE,{"disambiguationData":[TD([[makeQuery(id+"F7.imprint","IMPRINT",EDGE,{"derivedFrom":subQ3}),1.0]])]});}
            extrude(context, id + "F8", {"entities" : qUnion([Q0, Q1, Q2, Q3]), "depth" : 5 * mm});
        }
        {
            var Q0;
            {var subQ11=sQuery(id+"F7.wireOp",EDGE,"E72.bottom");Q0=makeQuery(id+"F7.imprint","IMPRINT",FACE,{"disambiguationData":[TD([[makeQuery(id+"F7.imprint","IMPRINT",EDGE,{"derivedFrom":subQ11}),-1.0]])]});}
            var Q1;
            {var subQ5=sQuery(id+"F7.wireOp",EDGE,"E73.right");Q1=makeQuery(id+"F7.imprint","IMPRINT",FACE,{"disambiguationData":[TD([[makeQuery(id+"F7.imprint","IMPRINT",EDGE,{"derivedFrom":subQ5}),-1.0]])]});}
            var Q2;
            {var subQ5=sQuery(id+"F7.wireOp",EDGE,"E74.left");Q2=makeQuery(id+"F7.imprint","IMPRINT",FACE,{"disambiguationData":[TD([[makeQuery(id+"F7.imprint","IMPRINT",EDGE,{"derivedFrom":subQ5}),1.0]])]});}
            var Q3;
            {var subQ0=sQuery(id+"F7.wireOp",EDGE,"E74.bottom");Q3=makeQuery(id+"F7.imprint","IMPRINT",FACE,{"disambiguationData":[TD([[makeQuery(id+"F7.imprint","IMPRINT",EDGE,{"derivedFrom":subQ0}),-1.0]])]});}
            var Q4;
            {var subQ2=sQuery(id+"F7.wireOp",EDGE,"E72.top");Q4=makeQuery(id+"F7.imprint","IMPRINT",FACE,{"disambiguationData":[TD([[makeQuery(id+"F7.imprint","IMPRINT",EDGE,{"derivedFrom":subQ2}),1.0]])]});}
            var Q5;
            {var subQ0=sQuery(id+"F7.wireOp",EDGE,"E73.bottom");Q5=makeQuery(id+"F7.imprint","IMPRINT",FACE,{"disambiguationData":[TD([[makeQuery(id+"F7.imprint","IMPRINT",EDGE,{"derivedFrom":subQ0}),-1.0]])]});}
            extrude(context, id + "F9", {"entities" : qUnion([Q0, Q1, Q2, Q3, Q4, Q5]), "depth" : 1 * mm});
        }
        {
            var Q0;
            {var subQ5=sQuery(id+"F7.wireOp",EDGE,"E74.right");Q0=makeQuery(id+"F7.imprint","IMPRINT",FACE,{"disambiguationData":[TD([[makeQuery(id+"F7.imprint","IMPRINT",EDGE,{"derivedFrom":subQ5}),-1.0]])]});}
            var Q1;
            {var subQ5=sQuery(id+"F7.wireOp",EDGE,"E74.left");Q1=makeQuery(id+"F7.imprint","IMPRINT",FACE,{"disambiguationData":[TD([[makeQuery(id+"F7.imprint","IMPRINT",EDGE,{"derivedFrom":subQ5}),1.0]])]});}
            var Q2;
            {var subQ5=sQuery(id+"F7.wireOp",EDGE,"E73.right");Q2=makeQuery(id+"F7.imprint","IMPRINT",FACE,{"disambiguationData":[TD([[makeQuery(id+"F7.imprint","IMPRINT",EDGE,{"derivedFrom":subQ5}),-1.0]])]});}
            var Q3;
            {var subQ5=sQuery(id+"F7.wireOp",EDGE,"E73.left");Q3=makeQuery(id+"F7.imprint","IMPRINT",FACE,{"disambiguationData":[TD([[makeQuery(id+"F7.imprint","IMPRINT",EDGE,{"derivedFrom":subQ5}),1.0]])]});}
            extrude(context, id + "F10", {"entities" : qUnion([Q0, Q1, Q2, Q3]), "operationType" : NewBodyOperationType.ADD, "oppositeDirection" : true, "depth" : 6.95 * mm});
        }
        {
            var Q0;
            Q0=makeQuery(id+"F9.opExtrude","CAP_FACE",FACE,{"disambiguationData":[OSD([sQuery(id+"F7.wireOp",EDGE,"E72.bottom"),sQuery(id+"F7.wireOp",EDGE,"E72.top"),sQuery(id+"F7.wireOp",EDGE,"E72.left"),sQuery(id+"F7.wireOp",EDGE,"E72.right"),sQuery(id+"F7.wireOp",EDGE,"E73.left"),sQuery(id+"F7.wireOp",EDGE,"E74.right"),sQuery(id+"F7.wireOp",EDGE,"E75.bottom"),sQuery(id+"F7.wireOp",EDGE,"E75.top"),sQuery(id+"F7.wireOp",EDGE,"E75.left"),sQuery(id+"F7.wireOp",EDGE,"E75.right")])],"isStart":false});
            var sketch = newSketch(context, id + "F11", { "sketchPlane" : qUnion([Q0])});
            skPoint(sketch, "E76.0", {"position": v(-121.72, 49.3) * mm});
            skLineSegment(sketch, "E77.bottom", {"start": v(-112.62, 40.2) * mm, "end": v(-130.82, 40.2) * mm});
            skLineSegment(sketch, "E77.top", {"start": v(-112.62, 58.4) * mm, "end": v(-130.82, 58.4) * mm});
            skLineSegment(sketch, "E77.left", {"start": v(-112.62, 40.2) * mm, "end": v(-112.62, 58.4) * mm});
            skLineSegment(sketch, "E77.right", {"start": v(-130.82, 40.2) * mm, "end": v(-130.82, 58.4) * mm});
            skLineSegment(sketch, "E78.0", {"start": v(-131.82, 39.2) * mm, "end": v(-131.82, 59.4) * mm});
            skLineSegment(sketch, "E78.1", {"start": v(-111.62, 39.2) * mm, "end": v(-131.82, 39.2) * mm});
            skLineSegment(sketch, "E78.2", {"start": v(-111.62, 39.2) * mm, "end": v(-111.62, 59.4) * mm});
            skLineSegment(sketch, "E78.3", {"start": v(-111.62, 59.4) * mm, "end": v(-131.82, 59.4) * mm});
            skSolve(sketch);
        }
        {
            var Q0;
            Q0=makeQuery(id+"F11.imprint","IMPRINT",FACE,{"disambiguationData":[TD([[makeQuery(id+"F11.imprint","IMPRINT",EDGE,{"derivedFrom":sQuery(id+"F11.wireOp",EDGE,"E77.bottom")}),1.0]])]});
            extrude(context, id + "F12", {"entities" : qUnion([Q0]), "operationType" : NewBodyOperationType.ADD, "depth" : 5 * mm});
        }
        {
            var Q0;
            Q0=makeQuery(id+"F6.boolean.opBoolean","MERGE",FACE,{"derivedFrom":[makeQuery(id+"F4.boolean.opBoolean","COPY",FACE,{"derivedFrom":makeQuery(id+"F4.opExtrude","CAP_FACE",FACE,{"disambiguationData":[OSD([sQuery(id+"F3.wireOp",EDGE,"E53.bottom"),sQuery(id+"F3.wireOp",EDGE,"E53.top"),sQuery(id+"F3.wireOp",EDGE,"E53.left"),sQuery(id+"F3.wireOp",EDGE,"E53.right")])],"isStart":false})}),makeQuery(id+"F6.opExtrude","CAP_FACE",FACE,{"disambiguationData":[OSD([sQuery(id+"F5.wireOp",EDGE,"E58.bottom"),sQuery(id+"F5.wireOp",EDGE,"E58.top"),sQuery(id+"F5.wireOp",EDGE,"E58.left"),sQuery(id+"F5.wireOp",EDGE,"E58.right")])],"isStart":false}),makeQuery(id+"F6.opExtrude","CAP_FACE",FACE,{"disambiguationData":[OSD([sQuery(id+"F5.wireOp",EDGE,"E60.bottom"),sQuery(id+"F5.wireOp",EDGE,"E60.top"),sQuery(id+"F5.wireOp",EDGE,"E60.left"),sQuery(id+"F5.wireOp",EDGE,"E60.right")])],"isStart":false})]});
            var sketch = newSketch(context, id + "F13", { "sketchPlane" : qUnion([Q0])});
            skPoint(sketch, "E79.0", {"position": v(-111.5, 3.96) * mm});
            skLineSegment(sketch, "E80.bottom", {"start": v(-108.5, 0.96) * mm, "end": v(-114.5, 0.96) * mm});
            skLineSegment(sketch, "E80.top", {"start": v(-108.5, 6.96) * mm, "end": v(-114.5, 6.96) * mm});
            skLineSegment(sketch, "E80.left", {"start": v(-108.5, 0.96) * mm, "end": v(-108.5, 6.96) * mm});
            skLineSegment(sketch, "E80.right", {"start": v(-114.5, 0.96) * mm, "end": v(-114.5, 6.96) * mm});
            skSolve(sketch);
        }
        {
            var Q0;
            {var subQ0=sQuery(id+"F13.wireOp",EDGE,"E80.top");Q0=makeQuery(id+"F13.imprint","IMPRINT",FACE,{"disambiguationData":[TD([[makeQuery(id+"F13.imprint","IMPRINT",EDGE,{"derivedFrom":subQ0}),1.0]])]});}
            var Q1;
            {var subQ0=sQuery(id+"F13.wireOp",EDGE,"E80.left");var subQ1=makeQuery(id+"F4.opExtrude","CAP_FACE",FACE,{"disambiguationData":[OSD([sQuery(id+"F3.wireOp",EDGE,"E53.bottom"),sQuery(id+"F3.wireOp",EDGE,"E53.top"),sQuery(id+"F3.wireOp",EDGE,"E53.left"),sQuery(id+"F3.wireOp",EDGE,"E53.right")])],"isStart":false});var subQ2=sQuery(id+"F0.wireOp",EDGE,"E33.trimOffspring");var subQ3=makeQuery(id+"F4.boolean.opBoolean","INTERSECT",EDGE,{"derivedFrom":[makeQuery(id+"F2.boolean.opBoolean","MERGE",FACE,{"derivedFrom":[makeQuery(id+"F1.opExtrude","SWEPT_FACE",FACE,{"disambiguationData":[OSD([subQ2])]}),makeQuery(id+"F2.opExtrude","SWEPT_FACE",FACE,{"disambiguationData":[OSD([subQ2])]})]}),subQ1]});var subQ4=makeQuery(id+"F13.imprint","INTERSECT",VERTEX,{"derivedFrom":[subQ3,subQ0]});Q1=makeQuery(id+"F13.imprint","IMPRINT",FACE,{"disambiguationData":[TD([[makeQuery(id+"F13.imprint","IMPRINT",EDGE,{"disambiguationData":[TD([[subQ4,-1.0]])],"derivedFrom":subQ0}),1.0]])]});}
            var Q2;
            {var subQ0=sQuery(id+"F13.wireOp",EDGE,"E80.bottom");Q2=makeQuery(id+"F13.imprint","IMPRINT",FACE,{"disambiguationData":[TD([[makeQuery(id+"F13.imprint","IMPRINT",EDGE,{"derivedFrom":subQ0}),-1.0]])]});}
            extrude(context, id + "F14", {"entities" : qUnion([Q0, Q1, Q2]), "operationType" : NewBodyOperationType.ADD, "depth" : 10 * mm});
        }
    });
